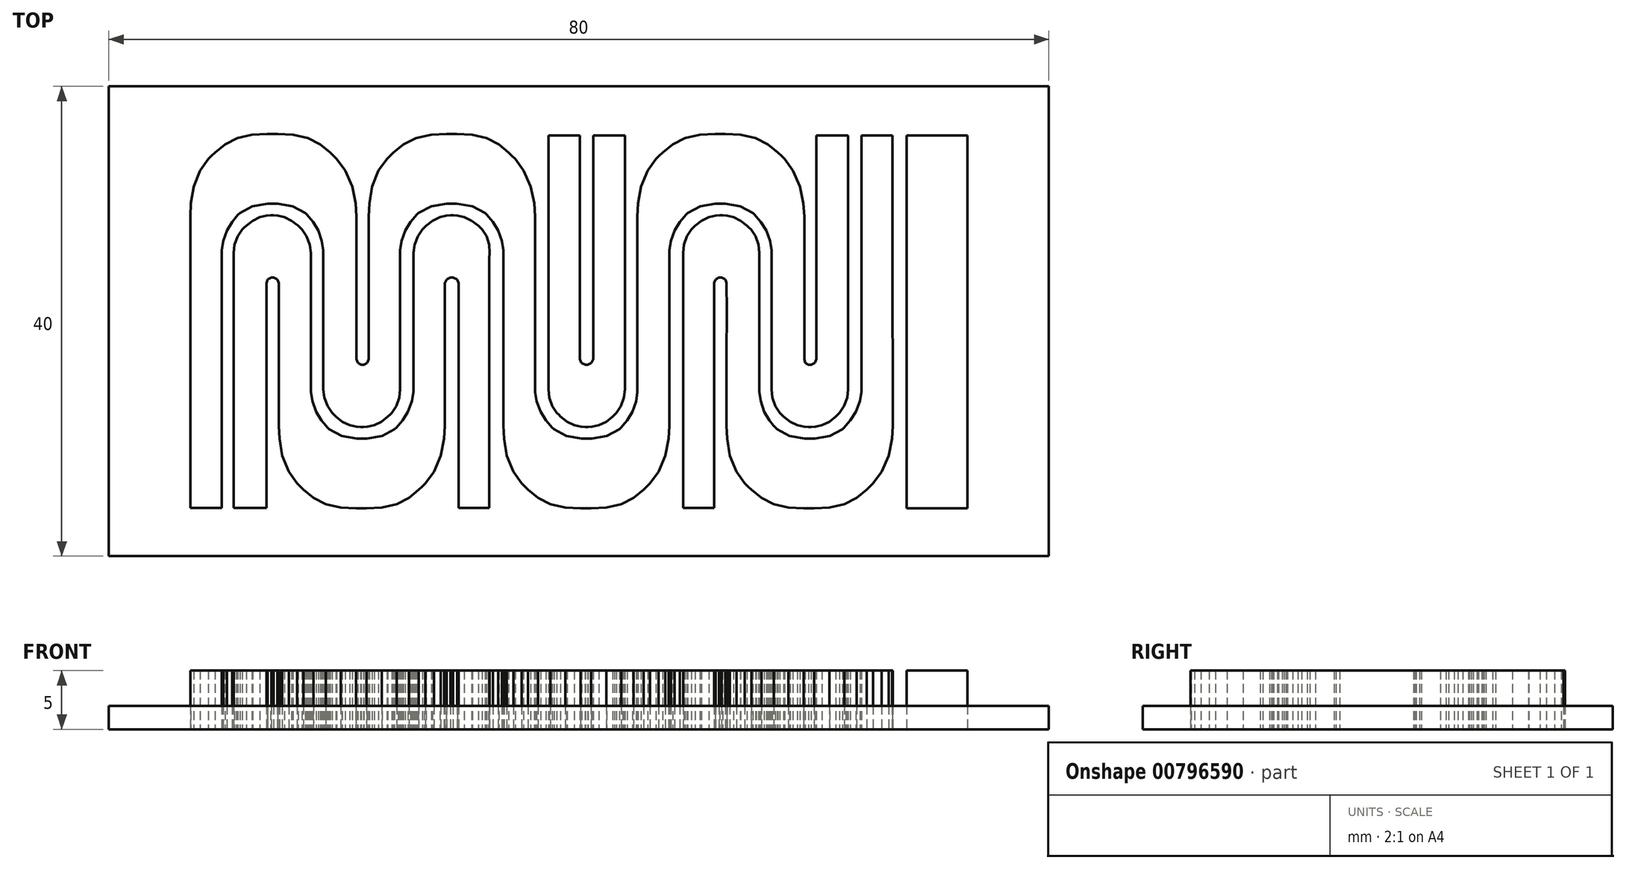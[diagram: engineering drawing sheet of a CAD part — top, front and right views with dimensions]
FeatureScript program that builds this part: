
annotation { "Feature Type Name" : "Feature", "Feature Type Description" : "" }
export const myFeature = defineFeature(function(context is Context, id is Id, definition is map)
    precondition{}
    {
        {
            var Q0;
            Q0=qCreatedBy(makeId("Top.planeOp"),FACE);
            var sketch = newSketch(context, id + "F0", { "sketchPlane" : qUnion([Q0])});
            skLineSegment(sketch, "E0.bottom", {"start": v(40, -20) * mm, "end": v(-40, -20) * mm});
            skLineSegment(sketch, "E0.top", {"start": v(40, 20) * mm, "end": v(-40, 20) * mm});
            skLineSegment(sketch, "E0.left", {"start": v(40, -20) * mm, "end": v(40, 20) * mm});
            skLineSegment(sketch, "E0.right", {"start": v(-40, -20) * mm, "end": v(-40, 20) * mm});
            skPoint(sketch, "E0.middle", {"position": v(0, 0) * mm});
            skSolve(sketch);
        }
        {
            var Q0;
            Q0 = qSketchRegion(id + "F0", true);
            extrude(context, id + "F1", {"entities" : qUnion([Q0]), "depth" : 2 * mm, "offsetDistance" : 25 * mm});
        }
        {
            var Q0;
            Q0=qCreatedBy(makeId("Top.planeOp"),FACE);
            var sketch = newSketch(context, id + "F2", { "sketchPlane" : qUnion([Q0])});
            skLineSegment(sketch, "E1", {"start": v(7.72, -8.54) * mm, "end": v(7.72, -4.96) * mm});
            skLineSegment(sketch, "E2", {"start": v(7.72, -4.96) * mm, "end": v(7.72, 3.1) * mm});
            skLineSegment(sketch, "E3", {"start": v(7.72, 3.1) * mm, "end": v(7.72, 5.78) * mm});
            skLineSegment(sketch, "E4", {"start": v(7.72, 5.78) * mm, "end": v(7.72, 6.04) * mm});
            skLineSegment(sketch, "E5", {"start": v(7.72, 6.04) * mm, "end": v(7.84, 6.84) * mm});
            skLineSegment(sketch, "E6", {"start": v(7.84, 6.84) * mm, "end": v(8.15, 7.73) * mm});
            skLineSegment(sketch, "E7", {"start": v(8.15, 7.73) * mm, "end": v(8.6, 8.46) * mm});
            skLineSegment(sketch, "E8", {"start": v(8.6, 8.46) * mm, "end": v(8.96, 8.9) * mm});
            skLineSegment(sketch, "E9", {"start": v(8.96, 8.9) * mm, "end": v(9.1, 9.04) * mm});
            skLineSegment(sketch, "E10", {"start": v(9.1, 9.04) * mm, "end": v(9.27, 9.21) * mm});
            skLineSegment(sketch, "E11", {"start": v(9.27, 9.21) * mm, "end": v(10.33, 9.79) * mm});
            skLineSegment(sketch, "E12", {"start": v(10.33, 9.79) * mm, "end": v(11.61, 10.02) * mm});
            skLineSegment(sketch, "E13", {"start": v(11.61, 10.02) * mm, "end": v(12.04, 10.02) * mm});
            skLineSegment(sketch, "E14", {"start": v(12.04, 10.02) * mm, "end": v(12.47, 10.02) * mm});
            skLineSegment(sketch, "E15", {"start": v(12.47, 10.02) * mm, "end": v(13.75, 9.79) * mm});
            skLineSegment(sketch, "E16", {"start": v(13.75, 9.79) * mm, "end": v(14.81, 9.21) * mm});
            skLineSegment(sketch, "E17", {"start": v(14.81, 9.21) * mm, "end": v(14.98, 9.04) * mm});
            skLineSegment(sketch, "E18", {"start": v(14.98, 9.04) * mm, "end": v(15.12, 8.9) * mm});
            skLineSegment(sketch, "E19", {"start": v(15.12, 8.9) * mm, "end": v(15.5, 8.46) * mm});
            skLineSegment(sketch, "E20", {"start": v(15.5, 8.46) * mm, "end": v(15.96, 7.73) * mm});
            skLineSegment(sketch, "E21", {"start": v(15.96, 7.73) * mm, "end": v(16.3, 6.84) * mm});
            skLineSegment(sketch, "E22", {"start": v(16.3, 6.84) * mm, "end": v(16.42, 6.04) * mm});
            skLineSegment(sketch, "E23", {"start": v(16.42, 6.04) * mm, "end": v(16.42, 5.78) * mm});
            skLineSegment(sketch, "E24", {"start": v(16.42, 5.78) * mm, "end": v(16.42, 3.05) * mm});
            skLineSegment(sketch, "E25", {"start": v(16.42, 3.05) * mm, "end": v(16.42, -3.1) * mm});
            skLineSegment(sketch, "E26", {"start": v(16.42, -3.1) * mm, "end": v(16.42, -5.15) * mm});
            skLineSegment(sketch, "E27", {"start": v(16.42, -5.15) * mm, "end": v(16.42, -5.3) * mm});
            skLineSegment(sketch, "E28", {"start": v(16.42, -5.3) * mm, "end": v(16.42, -5.79) * mm});
            skLineSegment(sketch, "E29", {"start": v(16.42, -5.79) * mm, "end": v(16.48, -6.49) * mm});
            skLineSegment(sketch, "E30", {"start": v(16.48, -6.49) * mm, "end": v(16.73, -7.22) * mm});
            skLineSegment(sketch, "E31", {"start": v(16.73, -7.22) * mm, "end": v(17.11, -7.81) * mm});
            skLineSegment(sketch, "E32", {"start": v(17.11, -7.81) * mm, "end": v(17.28, -7.97) * mm});
            skLineSegment(sketch, "E33", {"start": v(17.28, -7.97) * mm, "end": v(17.44, -8.13) * mm});
            skLineSegment(sketch, "E34", {"start": v(17.44, -8.13) * mm, "end": v(17.98, -8.55) * mm});
            skLineSegment(sketch, "E35", {"start": v(17.98, -8.55) * mm, "end": v(18.61, -8.86) * mm});
            skLineSegment(sketch, "E36", {"start": v(18.61, -8.86) * mm, "end": v(19.17, -8.98) * mm});
            skLineSegment(sketch, "E37", {"start": v(19.17, -8.98) * mm, "end": v(19.53, -9) * mm});
            skLineSegment(sketch, "E38", {"start": v(19.53, -9) * mm, "end": v(19.66, -9) * mm});
            skLineSegment(sketch, "E39", {"start": v(19.66, -9) * mm, "end": v(19.78, -9) * mm});
            skLineSegment(sketch, "E40", {"start": v(19.78, -9) * mm, "end": v(20.14, -8.98) * mm});
            skLineSegment(sketch, "E41", {"start": v(20.14, -8.98) * mm, "end": v(20.7, -8.86) * mm});
            skLineSegment(sketch, "E42", {"start": v(20.7, -8.86) * mm, "end": v(21.32, -8.55) * mm});
            skLineSegment(sketch, "E43", {"start": v(21.32, -8.55) * mm, "end": v(21.86, -8.13) * mm});
            skLineSegment(sketch, "E44", {"start": v(21.86, -8.13) * mm, "end": v(22.02, -7.97) * mm});
            skLineSegment(sketch, "E45", {"start": v(22.02, -7.97) * mm, "end": v(22.18, -7.81) * mm});
            skLineSegment(sketch, "E46", {"start": v(22.18, -7.81) * mm, "end": v(22.58, -7.22) * mm});
            skLineSegment(sketch, "E47", {"start": v(22.58, -7.22) * mm, "end": v(22.85, -6.49) * mm});
            skLineSegment(sketch, "E48", {"start": v(22.85, -6.49) * mm, "end": v(22.92, -5.79) * mm});
            skLineSegment(sketch, "E49", {"start": v(22.92, -5.79) * mm, "end": v(22.93, -5.3) * mm});
            skLineSegment(sketch, "E50", {"start": v(22.93, -5.3) * mm, "end": v(22.93, -5.15) * mm});
            skLineSegment(sketch, "E51", {"start": v(22.93, -5.15) * mm, "end": v(22.93, 0.1) * mm});
            skLineSegment(sketch, "E52", {"start": v(22.93, 0.1) * mm, "end": v(22.93, 11.89) * mm});
            skLineSegment(sketch, "E53", {"start": v(22.93, 11.89) * mm, "end": v(22.93, 15.82) * mm});
            skLineSegment(sketch, "E54", {"start": v(22.93, 15.82) * mm, "end": v(22.25, 15.82) * mm});
            skLineSegment(sketch, "E55", {"start": v(22.25, 15.82) * mm, "end": v(20.73, 15.82) * mm});
            skLineSegment(sketch, "E56", {"start": v(20.73, 15.82) * mm, "end": v(20.22, 15.82) * mm});
            skLineSegment(sketch, "E57", {"start": v(20.22, 15.82) * mm, "end": v(20.22, 13.45) * mm});
            skLineSegment(sketch, "E58", {"start": v(20.22, 13.45) * mm, "end": v(20.22, 6.35) * mm});
            skLineSegment(sketch, "E59", {"start": v(20.22, 6.35) * mm, "end": v(20.22, -0.75) * mm});
            skLineSegment(sketch, "E60", {"start": v(20.22, -0.75) * mm, "end": v(20.22, -3.12) * mm});
            skLineSegment(sketch, "E61", {"start": v(20.22, -3.12) * mm, "end": v(20.22, -3.22) * mm});
            skLineSegment(sketch, "E62", {"start": v(20.22, -3.22) * mm, "end": v(20.08, -3.54) * mm});
            skLineSegment(sketch, "E63", {"start": v(20.08, -3.54) * mm, "end": v(19.76, -3.71) * mm});
            skLineSegment(sketch, "E64", {"start": v(19.76, -3.71) * mm, "end": v(19.66, -3.71) * mm});
            skLineSegment(sketch, "E65", {"start": v(19.66, -3.71) * mm, "end": v(19.56, -3.71) * mm});
            skLineSegment(sketch, "E66", {"start": v(19.56, -3.71) * mm, "end": v(19.28, -3.54) * mm});
            skLineSegment(sketch, "E67", {"start": v(19.28, -3.54) * mm, "end": v(19.2, -3.22) * mm});
            skLineSegment(sketch, "E68", {"start": v(19.2, -3.22) * mm, "end": v(19.2, -3.12) * mm});
            skLineSegment(sketch, "E69", {"start": v(19.2, -3.12) * mm, "end": v(19.2, -2.43) * mm});
            skLineSegment(sketch, "E70", {"start": v(19.2, -2.43) * mm, "end": v(19.2, -0.37) * mm});
            skLineSegment(sketch, "E71", {"start": v(19.2, -0.37) * mm, "end": v(19.2, 2.78) * mm});
            skLineSegment(sketch, "E72", {"start": v(19.2, 2.78) * mm, "end": v(19.2, 5.9) * mm});
            skLineSegment(sketch, "E73", {"start": v(19.2, 5.9) * mm, "end": v(19.2, 7.9) * mm});
            skLineSegment(sketch, "E74", {"start": v(19.2, 7.9) * mm, "end": v(19.2, 8.57) * mm});
            skLineSegment(sketch, "E75", {"start": v(19.2, 8.57) * mm, "end": v(19.2, 8.93) * mm});
            skLineSegment(sketch, "E76", {"start": v(19.2, 8.93) * mm, "end": v(19.12, 10.03) * mm});
            skLineSegment(sketch, "E77", {"start": v(19.12, 10.03) * mm, "end": v(18.83, 11.47) * mm});
            skLineSegment(sketch, "E78", {"start": v(18.83, 11.47) * mm, "end": v(18.23, 12.84) * mm});
            skLineSegment(sketch, "E79", {"start": v(18.23, 12.84) * mm, "end": v(17.5, 13.82) * mm});
            skLineSegment(sketch, "E80", {"start": v(17.5, 13.82) * mm, "end": v(17.22, 14.1) * mm});
            skLineSegment(sketch, "E81", {"start": v(17.22, 14.1) * mm, "end": v(16.95, 14.35) * mm});
            skLineSegment(sketch, "E82", {"start": v(16.95, 14.35) * mm, "end": v(16.1, 15.05) * mm});
            skLineSegment(sketch, "E83", {"start": v(16.1, 15.05) * mm, "end": v(15.04, 15.6) * mm});
            skLineSegment(sketch, "E84", {"start": v(15.04, 15.6) * mm, "end": v(13.78, 15.87) * mm});
            skLineSegment(sketch, "E85", {"start": v(13.78, 15.87) * mm, "end": v(12.47, 15.94) * mm});
            skLineSegment(sketch, "E86", {"start": v(12.47, 15.94) * mm, "end": v(12.04, 15.94) * mm});
            skLineSegment(sketch, "E87", {"start": v(12.04, 15.94) * mm, "end": v(11.6, 15.94) * mm});
            skLineSegment(sketch, "E88", {"start": v(11.6, 15.94) * mm, "end": v(10.3, 15.87) * mm});
            skLineSegment(sketch, "E89", {"start": v(10.3, 15.87) * mm, "end": v(9.04, 15.6) * mm});
            skLineSegment(sketch, "E90", {"start": v(9.04, 15.6) * mm, "end": v(7.99, 15.05) * mm});
            skLineSegment(sketch, "E91", {"start": v(7.99, 15.05) * mm, "end": v(7.13, 14.35) * mm});
            skLineSegment(sketch, "E92", {"start": v(7.13, 14.35) * mm, "end": v(6.86, 14.1) * mm});
            skLineSegment(sketch, "E93", {"start": v(6.86, 14.1) * mm, "end": v(6.57, 13.82) * mm});
            skLineSegment(sketch, "E94", {"start": v(6.57, 13.82) * mm, "end": v(5.87, 12.84) * mm});
            skLineSegment(sketch, "E95", {"start": v(5.87, 12.84) * mm, "end": v(5.3, 11.47) * mm});
            skLineSegment(sketch, "E96", {"start": v(5.3, 11.47) * mm, "end": v(5.05, 10.03) * mm});
            skLineSegment(sketch, "E97", {"start": v(5.05, 10.03) * mm, "end": v(4.99, 8.93) * mm});
            skLineSegment(sketch, "E98", {"start": v(4.99, 8.93) * mm, "end": v(4.99, 8.57) * mm});
            skLineSegment(sketch, "E99", {"start": v(4.99, 8.57) * mm, "end": v(4.99, 8.14) * mm});
            skLineSegment(sketch, "E100", {"start": v(4.99, 8.14) * mm, "end": v(4.99, 6.85) * mm});
            skLineSegment(sketch, "E101", {"start": v(4.99, 6.85) * mm, "end": v(4.99, 4.77) * mm});
            skLineSegment(sketch, "E102", {"start": v(4.99, 4.77) * mm, "end": v(4.99, 2.5) * mm});
            skLineSegment(sketch, "E103", {"start": v(4.99, 2.5) * mm, "end": v(4.99, 0.23) * mm});
            skLineSegment(sketch, "E104", {"start": v(4.99, 0.23) * mm, "end": v(4.99, -1.9) * mm});
            skLineSegment(sketch, "E105", {"start": v(4.99, -1.9) * mm, "end": v(4.99, -3.73) * mm});
            skLineSegment(sketch, "E106", {"start": v(4.99, -3.73) * mm, "end": v(4.99, -5.07) * mm});
            skLineSegment(sketch, "E107", {"start": v(4.99, -5.07) * mm, "end": v(4.99, -5.58) * mm});
            skLineSegment(sketch, "E108", {"start": v(4.99, -5.58) * mm, "end": v(4.99, -5.75) * mm});
            skLineSegment(sketch, "E109", {"start": v(4.99, -5.75) * mm, "end": v(4.99, -6.01) * mm});
            skLineSegment(sketch, "E110", {"start": v(4.99, -6.01) * mm, "end": v(4.87, -6.8) * mm});
            skLineSegment(sketch, "E111", {"start": v(4.87, -6.8) * mm, "end": v(4.55, -7.7) * mm});
            skLineSegment(sketch, "E112", {"start": v(4.55, -7.7) * mm, "end": v(4.11, -8.44) * mm});
            skLineSegment(sketch, "E113", {"start": v(4.11, -8.44) * mm, "end": v(3.75, -8.9) * mm});
            skLineSegment(sketch, "E114", {"start": v(3.75, -8.9) * mm, "end": v(3.61, -9.03) * mm});
            skLineSegment(sketch, "E115", {"start": v(3.61, -9.03) * mm, "end": v(3.44, -9.2) * mm});
            skLineSegment(sketch, "E116", {"start": v(3.44, -9.2) * mm, "end": v(2.37, -9.77) * mm});
            skLineSegment(sketch, "E117", {"start": v(2.37, -9.77) * mm, "end": v(1.1, -10) * mm});
            skLineSegment(sketch, "E118", {"start": v(1.1, -10) * mm, "end": v(0.66, -10) * mm});
            skLineSegment(sketch, "E119", {"start": v(0.66, -10) * mm, "end": v(0.23, -10) * mm});
            skLineSegment(sketch, "E120", {"start": v(0.23, -10) * mm, "end": v(-1.06, -9.77) * mm});
            skLineSegment(sketch, "E121", {"start": v(-1.06, -9.77) * mm, "end": v(-2.11, -9.2) * mm});
            skLineSegment(sketch, "E122", {"start": v(-2.11, -9.2) * mm, "end": v(-2.28, -9.03) * mm});
            skLineSegment(sketch, "E123", {"start": v(-2.28, -9.03) * mm, "end": v(-2.42, -8.9) * mm});
            skLineSegment(sketch, "E124", {"start": v(-2.42, -8.9) * mm, "end": v(-2.8, -8.44) * mm});
            skLineSegment(sketch, "E125", {"start": v(-2.8, -8.44) * mm, "end": v(-3.26, -7.7) * mm});
            skLineSegment(sketch, "E126", {"start": v(-3.26, -7.7) * mm, "end": v(-3.6, -6.8) * mm});
            skLineSegment(sketch, "E127", {"start": v(-3.6, -6.8) * mm, "end": v(-3.72, -6.01) * mm});
            skLineSegment(sketch, "E128", {"start": v(-3.72, -6.01) * mm, "end": v(-3.72, -5.75) * mm});
            skLineSegment(sketch, "E129", {"start": v(-3.72, -5.75) * mm, "end": v(-3.72, -2.17) * mm});
            skLineSegment(sketch, "E130", {"start": v(-3.72, -2.17) * mm, "end": v(-3.72, 5.89) * mm});
            skLineSegment(sketch, "E131", {"start": v(-3.72, 5.89) * mm, "end": v(-3.72, 8.58) * mm});
            skLineSegment(sketch, "E132", {"start": v(-3.72, 8.58) * mm, "end": v(-3.72, 8.94) * mm});
            skLineSegment(sketch, "E133", {"start": v(-3.72, 8.94) * mm, "end": v(-3.8, 10.04) * mm});
            skLineSegment(sketch, "E134", {"start": v(-3.8, 10.04) * mm, "end": v(-4.1, 11.48) * mm});
            skLineSegment(sketch, "E135", {"start": v(-4.1, 11.48) * mm, "end": v(-4.7, 12.84) * mm});
            skLineSegment(sketch, "E136", {"start": v(-4.7, 12.84) * mm, "end": v(-5.42, 13.82) * mm});
            skLineSegment(sketch, "E137", {"start": v(-5.42, 13.82) * mm, "end": v(-5.71, 14.1) * mm});
            skLineSegment(sketch, "E138", {"start": v(-5.71, 14.1) * mm, "end": v(-5.98, 14.35) * mm});
            skLineSegment(sketch, "E139", {"start": v(-5.98, 14.35) * mm, "end": v(-6.82, 15.05) * mm});
            skLineSegment(sketch, "E140", {"start": v(-6.82, 15.05) * mm, "end": v(-7.84, 15.6) * mm});
            skLineSegment(sketch, "E141", {"start": v(-7.84, 15.6) * mm, "end": v(-9.07, 15.87) * mm});
            skLineSegment(sketch, "E142", {"start": v(-9.07, 15.87) * mm, "end": v(-10.38, 15.94) * mm});
            skLineSegment(sketch, "E143", {"start": v(-10.38, 15.94) * mm, "end": v(-10.8, 15.94) * mm});
            skLineSegment(sketch, "E144", {"start": v(-10.8, 15.94) * mm, "end": v(-11.25, 15.94) * mm});
            skLineSegment(sketch, "E145", {"start": v(-11.25, 15.94) * mm, "end": v(-12.56, 15.87) * mm});
            skLineSegment(sketch, "E146", {"start": v(-12.56, 15.87) * mm, "end": v(-13.85, 15.6) * mm});
            skLineSegment(sketch, "E147", {"start": v(-13.85, 15.6) * mm, "end": v(-14.92, 15.05) * mm});
            skLineSegment(sketch, "E148", {"start": v(-14.92, 15.05) * mm, "end": v(-15.79, 14.35) * mm});
            skLineSegment(sketch, "E149", {"start": v(-15.79, 14.35) * mm, "end": v(-16.05, 14.1) * mm});
            skLineSegment(sketch, "E150", {"start": v(-16.05, 14.1) * mm, "end": v(-16.34, 13.82) * mm});
            skLineSegment(sketch, "E151", {"start": v(-16.34, 13.82) * mm, "end": v(-17.04, 12.84) * mm});
            skLineSegment(sketch, "E152", {"start": v(-17.04, 12.84) * mm, "end": v(-17.6, 11.48) * mm});
            skLineSegment(sketch, "E153", {"start": v(-17.6, 11.48) * mm, "end": v(-17.83, 10.04) * mm});
            skLineSegment(sketch, "E154", {"start": v(-17.83, 10.04) * mm, "end": v(-17.88, 8.94) * mm});
            skLineSegment(sketch, "E155", {"start": v(-17.88, 8.94) * mm, "end": v(-17.88, 8.58) * mm});
            skLineSegment(sketch, "E156", {"start": v(-17.88, 8.58) * mm, "end": v(-17.88, 5.65) * mm});
            skLineSegment(sketch, "E157", {"start": v(-17.88, 5.65) * mm, "end": v(-17.88, -0.93) * mm});
            skLineSegment(sketch, "E158", {"start": v(-17.88, -0.93) * mm, "end": v(-17.88, -3.12) * mm});
            skLineSegment(sketch, "E159", {"start": v(-17.88, -3.12) * mm, "end": v(-17.88, -3.22) * mm});
            skLineSegment(sketch, "E160", {"start": v(-17.88, -3.22) * mm, "end": v(-18, -3.54) * mm});
            skLineSegment(sketch, "E161", {"start": v(-18, -3.54) * mm, "end": v(-18.3, -3.71) * mm});
            skLineSegment(sketch, "E162", {"start": v(-18.3, -3.71) * mm, "end": v(-18.4, -3.71) * mm});
            skLineSegment(sketch, "E163", {"start": v(-18.4, -3.71) * mm, "end": v(-18.5, -3.71) * mm});
            skLineSegment(sketch, "E164", {"start": v(-18.5, -3.71) * mm, "end": v(-18.82, -3.54) * mm});
            skLineSegment(sketch, "E165", {"start": v(-18.82, -3.54) * mm, "end": v(-18.94, -3.22) * mm});
            skLineSegment(sketch, "E166", {"start": v(-18.94, -3.22) * mm, "end": v(-18.94, -3.12) * mm});
            skLineSegment(sketch, "E167", {"start": v(-18.94, -3.12) * mm, "end": v(-18.94, -0.2) * mm});
            skLineSegment(sketch, "E168", {"start": v(-18.94, -0.2) * mm, "end": v(-18.94, 6.38) * mm});
            skLineSegment(sketch, "E169", {"start": v(-18.94, 6.38) * mm, "end": v(-18.94, 8.58) * mm});
            skLineSegment(sketch, "E170", {"start": v(-18.94, 8.58) * mm, "end": v(-18.94, 8.94) * mm});
            skLineSegment(sketch, "E171", {"start": v(-18.94, 8.94) * mm, "end": v(-19, 10.04) * mm});
            skLineSegment(sketch, "E172", {"start": v(-19, 10.04) * mm, "end": v(-19.3, 11.47) * mm});
            skLineSegment(sketch, "E173", {"start": v(-19.3, 11.47) * mm, "end": v(-19.89, 12.84) * mm});
            skLineSegment(sketch, "E174", {"start": v(-19.89, 12.84) * mm, "end": v(-20.6, 13.82) * mm});
            skLineSegment(sketch, "E175", {"start": v(-20.6, 13.82) * mm, "end": v(-20.9, 14.1) * mm});
            skLineSegment(sketch, "E176", {"start": v(-20.9, 14.1) * mm, "end": v(-21.17, 14.35) * mm});
            skLineSegment(sketch, "E177", {"start": v(-21.17, 14.35) * mm, "end": v(-22.02, 15.05) * mm});
            skLineSegment(sketch, "E178", {"start": v(-22.02, 15.05) * mm, "end": v(-23.07, 15.6) * mm});
            skLineSegment(sketch, "E179", {"start": v(-23.07, 15.6) * mm, "end": v(-24.33, 15.87) * mm});
            skLineSegment(sketch, "E180", {"start": v(-24.33, 15.87) * mm, "end": v(-25.64, 15.94) * mm});
            skLineSegment(sketch, "E181", {"start": v(-25.64, 15.94) * mm, "end": v(-26.08, 15.94) * mm});
            skLineSegment(sketch, "E182", {"start": v(-26.08, 15.94) * mm, "end": v(-26.51, 15.94) * mm});
            skLineSegment(sketch, "E183", {"start": v(-26.51, 15.94) * mm, "end": v(-27.82, 15.87) * mm});
            skLineSegment(sketch, "E184", {"start": v(-27.82, 15.87) * mm, "end": v(-29.07, 15.6) * mm});
            skLineSegment(sketch, "E185", {"start": v(-29.07, 15.6) * mm, "end": v(-30.12, 15.05) * mm});
            skLineSegment(sketch, "E186", {"start": v(-30.12, 15.05) * mm, "end": v(-30.98, 14.35) * mm});
            skLineSegment(sketch, "E187", {"start": v(-30.98, 14.35) * mm, "end": v(-31.24, 14.1) * mm});
            skLineSegment(sketch, "E188", {"start": v(-31.24, 14.1) * mm, "end": v(-31.53, 13.82) * mm});
            skLineSegment(sketch, "E189", {"start": v(-31.53, 13.82) * mm, "end": v(-32.24, 12.84) * mm});
            skLineSegment(sketch, "E190", {"start": v(-32.24, 12.84) * mm, "end": v(-32.79, 11.47) * mm});
            skLineSegment(sketch, "E191", {"start": v(-32.79, 11.47) * mm, "end": v(-33.02, 10.04) * mm});
            skLineSegment(sketch, "E192", {"start": v(-33.02, 10.04) * mm, "end": v(-33.07, 8.94) * mm});
            skLineSegment(sketch, "E193", {"start": v(-33.07, 8.94) * mm, "end": v(-33.07, 8.58) * mm});
            skLineSegment(sketch, "E194", {"start": v(-33.07, 8.58) * mm, "end": v(-33.07, -15.9) * mm});
            skLineSegment(sketch, "E195", {"start": v(-33.07, -15.9) * mm, "end": v(-32.4, -15.9) * mm});
            skLineSegment(sketch, "E196", {"start": v(-32.4, -15.9) * mm, "end": v(-30.9, -15.9) * mm});
            skLineSegment(sketch, "E197", {"start": v(-30.9, -15.9) * mm, "end": v(-30.4, -15.9) * mm});
            skLineSegment(sketch, "E198", {"start": v(-30.4, -15.9) * mm, "end": v(-30.4, -13.18) * mm});
            skLineSegment(sketch, "E199", {"start": v(-30.4, -13.18) * mm, "end": v(-30.4, -5.06) * mm});
            skLineSegment(sketch, "E200", {"start": v(-30.4, -5.06) * mm, "end": v(-30.4, 3.07) * mm});
            skLineSegment(sketch, "E201", {"start": v(-30.4, 3.07) * mm, "end": v(-30.4, 5.77) * mm});
            skLineSegment(sketch, "E202", {"start": v(-30.4, 5.77) * mm, "end": v(-30.4, 6.04) * mm});
            skLineSegment(sketch, "E203", {"start": v(-30.4, 6.04) * mm, "end": v(-30.27, 6.83) * mm});
            skLineSegment(sketch, "E204", {"start": v(-30.27, 6.83) * mm, "end": v(-29.96, 7.73) * mm});
            skLineSegment(sketch, "E205", {"start": v(-29.96, 7.73) * mm, "end": v(-29.52, 8.46) * mm});
            skLineSegment(sketch, "E206", {"start": v(-29.52, 8.46) * mm, "end": v(-29.15, 8.9) * mm});
            skLineSegment(sketch, "E207", {"start": v(-29.15, 8.9) * mm, "end": v(-29.01, 9.04) * mm});
            skLineSegment(sketch, "E208", {"start": v(-29.01, 9.04) * mm, "end": v(-28.85, 9.21) * mm});
            skLineSegment(sketch, "E209", {"start": v(-28.85, 9.21) * mm, "end": v(-27.78, 9.79) * mm});
            skLineSegment(sketch, "E210", {"start": v(-27.78, 9.79) * mm, "end": v(-26.5, 10.02) * mm});
            skLineSegment(sketch, "E211", {"start": v(-26.5, 10.02) * mm, "end": v(-26.07, 10.02) * mm});
            skLineSegment(sketch, "E212", {"start": v(-26.07, 10.02) * mm, "end": v(-25.64, 10.02) * mm});
            skLineSegment(sketch, "E213", {"start": v(-25.64, 10.02) * mm, "end": v(-24.35, 9.79) * mm});
            skLineSegment(sketch, "E214", {"start": v(-24.35, 9.79) * mm, "end": v(-23.29, 9.21) * mm});
            skLineSegment(sketch, "E215", {"start": v(-23.29, 9.21) * mm, "end": v(-23.12, 9.04) * mm});
            skLineSegment(sketch, "E216", {"start": v(-23.12, 9.04) * mm, "end": v(-22.98, 8.9) * mm});
            skLineSegment(sketch, "E217", {"start": v(-22.98, 8.9) * mm, "end": v(-22.62, 8.46) * mm});
            skLineSegment(sketch, "E218", {"start": v(-22.62, 8.46) * mm, "end": v(-22.18, 7.73) * mm});
            skLineSegment(sketch, "E219", {"start": v(-22.18, 7.73) * mm, "end": v(-21.87, 6.83) * mm});
            skLineSegment(sketch, "E220", {"start": v(-21.87, 6.83) * mm, "end": v(-21.75, 6.04) * mm});
            skLineSegment(sketch, "E221", {"start": v(-21.75, 6.04) * mm, "end": v(-21.75, 5.77) * mm});
            skLineSegment(sketch, "E222", {"start": v(-21.75, 5.77) * mm, "end": v(-21.75, 3.04) * mm});
            skLineSegment(sketch, "E223", {"start": v(-21.75, 3.04) * mm, "end": v(-21.75, -3.1) * mm});
            skLineSegment(sketch, "E224", {"start": v(-21.75, -3.1) * mm, "end": v(-21.75, -5.15) * mm});
            skLineSegment(sketch, "E225", {"start": v(-21.75, -5.15) * mm, "end": v(-21.75, -5.3) * mm});
            skLineSegment(sketch, "E226", {"start": v(-21.75, -5.3) * mm, "end": v(-21.75, -5.79) * mm});
            skLineSegment(sketch, "E227", {"start": v(-21.75, -5.79) * mm, "end": v(-21.66, -6.49) * mm});
            skLineSegment(sketch, "E228", {"start": v(-21.66, -6.49) * mm, "end": v(-21.39, -7.22) * mm});
            skLineSegment(sketch, "E229", {"start": v(-21.39, -7.22) * mm, "end": v(-21, -7.8) * mm});
            skLineSegment(sketch, "E230", {"start": v(-21, -7.8) * mm, "end": v(-20.83, -7.97) * mm});
            skLineSegment(sketch, "E231", {"start": v(-20.83, -7.97) * mm, "end": v(-20.67, -8.13) * mm});
            skLineSegment(sketch, "E232", {"start": v(-20.67, -8.13) * mm, "end": v(-20.12, -8.55) * mm});
            skLineSegment(sketch, "E233", {"start": v(-20.12, -8.55) * mm, "end": v(-19.5, -8.86) * mm});
            skLineSegment(sketch, "E234", {"start": v(-19.5, -8.86) * mm, "end": v(-18.94, -8.98) * mm});
            skLineSegment(sketch, "E235", {"start": v(-18.94, -8.98) * mm, "end": v(-18.58, -9) * mm});
            skLineSegment(sketch, "E236", {"start": v(-18.58, -9) * mm, "end": v(-18.46, -9) * mm});
            skLineSegment(sketch, "E237", {"start": v(-18.46, -9) * mm, "end": v(-18.34, -9) * mm});
            skLineSegment(sketch, "E238", {"start": v(-18.34, -9) * mm, "end": v(-17.98, -8.98) * mm});
            skLineSegment(sketch, "E239", {"start": v(-17.98, -8.98) * mm, "end": v(-17.42, -8.86) * mm});
            skLineSegment(sketch, "E240", {"start": v(-17.42, -8.86) * mm, "end": v(-16.8, -8.55) * mm});
            skLineSegment(sketch, "E241", {"start": v(-16.8, -8.55) * mm, "end": v(-16.25, -8.13) * mm});
            skLineSegment(sketch, "E242", {"start": v(-16.25, -8.13) * mm, "end": v(-16.09, -7.97) * mm});
            skLineSegment(sketch, "E243", {"start": v(-16.09, -7.97) * mm, "end": v(-15.93, -7.81) * mm});
            skLineSegment(sketch, "E244", {"start": v(-15.93, -7.81) * mm, "end": v(-15.53, -7.22) * mm});
            skLineSegment(sketch, "E245", {"start": v(-15.53, -7.22) * mm, "end": v(-15.28, -6.49) * mm});
            skLineSegment(sketch, "E246", {"start": v(-15.28, -6.49) * mm, "end": v(-15.2, -5.79) * mm});
            skLineSegment(sketch, "E247", {"start": v(-15.2, -5.79) * mm, "end": v(-15.2, -5.3) * mm});
            skLineSegment(sketch, "E248", {"start": v(-15.2, -5.3) * mm, "end": v(-15.2, -5.15) * mm});
            skLineSegment(sketch, "E249", {"start": v(-15.2, -5.15) * mm, "end": v(-15.2, -4.73) * mm});
            skLineSegment(sketch, "E250", {"start": v(-15.2, -4.73) * mm, "end": v(-15.2, -3.5) * mm});
            skLineSegment(sketch, "E251", {"start": v(-15.2, -3.5) * mm, "end": v(-15.2, -0.44) * mm});
            skLineSegment(sketch, "E252", {"start": v(-15.2, -0.44) * mm, "end": v(-15.2, 3) * mm});
            skLineSegment(sketch, "E253", {"start": v(-15.2, 3) * mm, "end": v(-15.2, 5.08) * mm});
            skLineSegment(sketch, "E254", {"start": v(-15.2, 5.08) * mm, "end": v(-15.2, 5.77) * mm});
            skLineSegment(sketch, "E255", {"start": v(-15.2, 5.77) * mm, "end": v(-15.2, 6.04) * mm});
            skLineSegment(sketch, "E256", {"start": v(-15.2, 6.04) * mm, "end": v(-15.08, 6.83) * mm});
            skLineSegment(sketch, "E257", {"start": v(-15.08, 6.83) * mm, "end": v(-14.77, 7.73) * mm});
            skLineSegment(sketch, "E258", {"start": v(-14.77, 7.73) * mm, "end": v(-14.32, 8.46) * mm});
            skLineSegment(sketch, "E259", {"start": v(-14.32, 8.46) * mm, "end": v(-13.96, 8.9) * mm});
            skLineSegment(sketch, "E260", {"start": v(-13.96, 8.9) * mm, "end": v(-13.82, 9.04) * mm});
            skLineSegment(sketch, "E261", {"start": v(-13.82, 9.04) * mm, "end": v(-13.65, 9.21) * mm});
            skLineSegment(sketch, "E262", {"start": v(-13.65, 9.21) * mm, "end": v(-12.56, 9.79) * mm});
            skLineSegment(sketch, "E263", {"start": v(-12.56, 9.79) * mm, "end": v(-11.25, 10.02) * mm});
            skLineSegment(sketch, "E264", {"start": v(-11.25, 10.02) * mm, "end": v(-10.8, 10.02) * mm});
            skLineSegment(sketch, "E265", {"start": v(-10.8, 10.02) * mm, "end": v(-10.38, 10.02) * mm});
            skLineSegment(sketch, "E266", {"start": v(-10.38, 10.02) * mm, "end": v(-9.07, 9.79) * mm});
            skLineSegment(sketch, "E267", {"start": v(-9.07, 9.79) * mm, "end": v(-7.98, 9.21) * mm});
            skLineSegment(sketch, "E268", {"start": v(-7.98, 9.21) * mm, "end": v(-7.81, 9.04) * mm});
            skLineSegment(sketch, "E269", {"start": v(-7.81, 9.04) * mm, "end": v(-7.68, 8.9) * mm});
            skLineSegment(sketch, "E270", {"start": v(-7.68, 8.9) * mm, "end": v(-7.3, 8.46) * mm});
            skLineSegment(sketch, "E271", {"start": v(-7.3, 8.46) * mm, "end": v(-6.86, 7.73) * mm});
            skLineSegment(sketch, "E272", {"start": v(-6.86, 7.73) * mm, "end": v(-6.54, 6.83) * mm});
            skLineSegment(sketch, "E273", {"start": v(-6.54, 6.83) * mm, "end": v(-6.42, 6.04) * mm});
            skLineSegment(sketch, "E274", {"start": v(-6.42, 6.04) * mm, "end": v(-6.42, 5.77) * mm});
            skLineSegment(sketch, "E275", {"start": v(-6.42, 5.77) * mm, "end": v(-6.42, 2.2) * mm});
            skLineSegment(sketch, "E276", {"start": v(-6.42, 2.2) * mm, "end": v(-6.42, -5.84) * mm});
            skLineSegment(sketch, "E277", {"start": v(-6.42, -5.84) * mm, "end": v(-6.42, -8.53) * mm});
            skLineSegment(sketch, "E278", {"start": v(-6.42, -8.53) * mm, "end": v(-6.42, -8.9) * mm});
            skLineSegment(sketch, "E279", {"start": v(-6.42, -8.9) * mm, "end": v(-6.37, -10) * mm});
            skLineSegment(sketch, "E280", {"start": v(-6.37, -10) * mm, "end": v(-6.12, -11.46) * mm});
            skLineSegment(sketch, "E281", {"start": v(-6.12, -11.46) * mm, "end": v(-5.57, -12.83) * mm});
            skLineSegment(sketch, "E282", {"start": v(-5.57, -12.83) * mm, "end": v(-4.87, -13.81) * mm});
            skLineSegment(sketch, "E283", {"start": v(-4.87, -13.81) * mm, "end": v(-4.58, -14.08) * mm});
            skLineSegment(sketch, "E284", {"start": v(-4.58, -14.08) * mm, "end": v(-4.32, -14.34) * mm});
            skLineSegment(sketch, "E285", {"start": v(-4.32, -14.34) * mm, "end": v(-3.46, -15.04) * mm});
            skLineSegment(sketch, "E286", {"start": v(-3.46, -15.04) * mm, "end": v(-2.4, -15.6) * mm});
            skLineSegment(sketch, "E287", {"start": v(-2.4, -15.6) * mm, "end": v(-1.15, -15.86) * mm});
            skLineSegment(sketch, "E288", {"start": v(-1.15, -15.86) * mm, "end": v(0.16, -15.93) * mm});
            skLineSegment(sketch, "E289", {"start": v(0.16, -15.93) * mm, "end": v(0.6, -15.93) * mm});
            skLineSegment(sketch, "E290", {"start": v(0.6, -15.93) * mm, "end": v(1.03, -15.93) * mm});
            skLineSegment(sketch, "E291", {"start": v(1.03, -15.93) * mm, "end": v(2.34, -15.86) * mm});
            skLineSegment(sketch, "E292", {"start": v(2.34, -15.86) * mm, "end": v(3.6, -15.6) * mm});
            skLineSegment(sketch, "E293", {"start": v(3.6, -15.6) * mm, "end": v(4.65, -15.04) * mm});
            skLineSegment(sketch, "E294", {"start": v(4.65, -15.04) * mm, "end": v(5.5, -14.34) * mm});
            skLineSegment(sketch, "E295", {"start": v(5.5, -14.34) * mm, "end": v(5.77, -14.08) * mm});
            skLineSegment(sketch, "E296", {"start": v(5.77, -14.08) * mm, "end": v(6.06, -13.81) * mm});
            skLineSegment(sketch, "E297", {"start": v(6.06, -13.81) * mm, "end": v(6.78, -12.83) * mm});
            skLineSegment(sketch, "E298", {"start": v(6.78, -12.83) * mm, "end": v(7.37, -11.46) * mm});
            skLineSegment(sketch, "E299", {"start": v(7.37, -11.46) * mm, "end": v(7.65, -10) * mm});
            skLineSegment(sketch, "E300", {"start": v(7.65, -10) * mm, "end": v(7.72, -8.9) * mm});
            skLineSegment(sketch, "E301", {"start": v(7.72, -8.9) * mm, "end": v(7.72, -8.54) * mm});
            skLineSegment(sketch, "E302", {"start": v(24.76, -14.08) * mm, "end": v(25.05, -13.81) * mm});
            skLineSegment(sketch, "E303", {"start": v(25.05, -13.81) * mm, "end": v(25.77, -12.83) * mm});
            skLineSegment(sketch, "E304", {"start": v(25.77, -12.83) * mm, "end": v(26.37, -11.46) * mm});
            skLineSegment(sketch, "E305", {"start": v(26.37, -11.46) * mm, "end": v(26.65, -10) * mm});
            skLineSegment(sketch, "E306", {"start": v(26.65, -10) * mm, "end": v(26.73, -8.9) * mm});
            skLineSegment(sketch, "E307", {"start": v(26.73, -8.9) * mm, "end": v(26.73, -8.54) * mm});
            skLineSegment(sketch, "E308", {"start": v(26.73, -8.54) * mm, "end": v(26.72, -6.55) * mm});
            skLineSegment(sketch, "E309", {"start": v(26.72, -6.55) * mm, "end": v(26.7, 3.64) * mm});
            skLineSegment(sketch, "E310", {"start": v(26.7, 3.64) * mm, "end": v(26.7, 12.77) * mm});
            skLineSegment(sketch, "E311", {"start": v(26.7, 12.77) * mm, "end": v(26.7, 15.82) * mm});
            skLineSegment(sketch, "E312", {"start": v(26.7, 15.82) * mm, "end": v(26.04, 15.82) * mm});
            skLineSegment(sketch, "E313", {"start": v(26.04, 15.82) * mm, "end": v(24.56, 15.82) * mm});
            skLineSegment(sketch, "E314", {"start": v(24.56, 15.82) * mm, "end": v(24.06, 15.82) * mm});
            skLineSegment(sketch, "E315", {"start": v(24.06, 15.82) * mm, "end": v(24.06, 13.12) * mm});
            skLineSegment(sketch, "E316", {"start": v(24.06, 13.12) * mm, "end": v(24.06, 5.04) * mm});
            skLineSegment(sketch, "E317", {"start": v(24.06, 5.04) * mm, "end": v(24.06, -3.04) * mm});
            skLineSegment(sketch, "E318", {"start": v(24.06, -3.04) * mm, "end": v(24.06, -5.74) * mm});
            skLineSegment(sketch, "E319", {"start": v(24.06, -5.74) * mm, "end": v(24.06, -6) * mm});
            skLineSegment(sketch, "E320", {"start": v(24.06, -6) * mm, "end": v(23.93, -6.8) * mm});
            skLineSegment(sketch, "E321", {"start": v(23.93, -6.8) * mm, "end": v(23.58, -7.7) * mm});
            skLineSegment(sketch, "E322", {"start": v(23.58, -7.7) * mm, "end": v(23.12, -8.44) * mm});
            skLineSegment(sketch, "E323", {"start": v(23.12, -8.44) * mm, "end": v(22.74, -8.9) * mm});
            skLineSegment(sketch, "E324", {"start": v(22.74, -8.9) * mm, "end": v(22.6, -9.03) * mm});
            skLineSegment(sketch, "E325", {"start": v(22.6, -9.03) * mm, "end": v(22.43, -9.2) * mm});
            skLineSegment(sketch, "E326", {"start": v(22.43, -9.2) * mm, "end": v(21.37, -9.77) * mm});
            skLineSegment(sketch, "E327", {"start": v(21.37, -9.77) * mm, "end": v(20.08, -10) * mm});
            skLineSegment(sketch, "E328", {"start": v(20.08, -10) * mm, "end": v(19.66, -10) * mm});
            skLineSegment(sketch, "E329", {"start": v(19.66, -10) * mm, "end": v(19.23, -10) * mm});
            skLineSegment(sketch, "E330", {"start": v(19.23, -10) * mm, "end": v(17.94, -9.77) * mm});
            skLineSegment(sketch, "E331", {"start": v(17.94, -9.77) * mm, "end": v(16.88, -9.2) * mm});
            skLineSegment(sketch, "E332", {"start": v(16.88, -9.2) * mm, "end": v(16.7, -9.03) * mm});
            skLineSegment(sketch, "E333", {"start": v(16.7, -9.03) * mm, "end": v(16.57, -8.9) * mm});
            skLineSegment(sketch, "E334", {"start": v(16.57, -8.9) * mm, "end": v(16.2, -8.44) * mm});
            skLineSegment(sketch, "E335", {"start": v(16.2, -8.44) * mm, "end": v(15.78, -7.7) * mm});
            skLineSegment(sketch, "E336", {"start": v(15.78, -7.7) * mm, "end": v(15.48, -6.8) * mm});
            skLineSegment(sketch, "E337", {"start": v(15.48, -6.8) * mm, "end": v(15.36, -6) * mm});
            skLineSegment(sketch, "E338", {"start": v(15.36, -6) * mm, "end": v(15.36, -5.74) * mm});
            skLineSegment(sketch, "E339", {"start": v(15.36, -5.74) * mm, "end": v(15.36, -4.37) * mm});
            skLineSegment(sketch, "E340", {"start": v(15.36, -4.37) * mm, "end": v(15.36, -0.27) * mm});
            skLineSegment(sketch, "E341", {"start": v(15.36, -0.27) * mm, "end": v(15.36, 3.82) * mm});
            skLineSegment(sketch, "E342", {"start": v(15.36, 3.82) * mm, "end": v(15.36, 5.18) * mm});
            skLineSegment(sketch, "E343", {"start": v(15.36, 5.18) * mm, "end": v(15.36, 5.34) * mm});
            skLineSegment(sketch, "E344", {"start": v(15.36, 5.34) * mm, "end": v(15.37, 5.82) * mm});
            skLineSegment(sketch, "E345", {"start": v(15.37, 5.82) * mm, "end": v(15.3, 6.51) * mm});
            skLineSegment(sketch, "E346", {"start": v(15.3, 6.51) * mm, "end": v(15.04, 7.24) * mm});
            skLineSegment(sketch, "E347", {"start": v(15.04, 7.24) * mm, "end": v(14.65, 7.82) * mm});
            skLineSegment(sketch, "E348", {"start": v(14.65, 7.82) * mm, "end": v(14.48, 7.98) * mm});
            skLineSegment(sketch, "E349", {"start": v(14.48, 7.98) * mm, "end": v(14.32, 8.14) * mm});
            skLineSegment(sketch, "E350", {"start": v(14.32, 8.14) * mm, "end": v(13.78, 8.56) * mm});
            skLineSegment(sketch, "E351", {"start": v(13.78, 8.56) * mm, "end": v(13.16, 8.87) * mm});
            skLineSegment(sketch, "E352", {"start": v(13.16, 8.87) * mm, "end": v(12.6, 9) * mm});
            skLineSegment(sketch, "E353", {"start": v(12.6, 9) * mm, "end": v(12.24, 9.02) * mm});
            skLineSegment(sketch, "E354", {"start": v(12.24, 9.02) * mm, "end": v(12.12, 9.02) * mm});
            skLineSegment(sketch, "E355", {"start": v(12.12, 9.02) * mm, "end": v(12, 9.02) * mm});
            skLineSegment(sketch, "E356", {"start": v(12, 9.02) * mm, "end": v(11.64, 9) * mm});
            skLineSegment(sketch, "E357", {"start": v(11.64, 9) * mm, "end": v(11.08, 8.87) * mm});
            skLineSegment(sketch, "E358", {"start": v(11.08, 8.87) * mm, "end": v(10.45, 8.56) * mm});
            skLineSegment(sketch, "E359", {"start": v(10.45, 8.56) * mm, "end": v(9.9, 8.14) * mm});
            skLineSegment(sketch, "E360", {"start": v(9.9, 8.14) * mm, "end": v(9.75, 7.98) * mm});
            skLineSegment(sketch, "E361", {"start": v(9.75, 7.98) * mm, "end": v(9.59, 7.82) * mm});
            skLineSegment(sketch, "E362", {"start": v(9.59, 7.82) * mm, "end": v(9.2, 7.24) * mm});
            skLineSegment(sketch, "E363", {"start": v(9.2, 7.24) * mm, "end": v(8.95, 6.51) * mm});
            skLineSegment(sketch, "E364", {"start": v(8.95, 6.51) * mm, "end": v(8.89, 5.82) * mm});
            skLineSegment(sketch, "E365", {"start": v(8.89, 5.82) * mm, "end": v(8.9, 5.34) * mm});
            skLineSegment(sketch, "E366", {"start": v(8.9, 5.34) * mm, "end": v(8.9, 5.18) * mm});
            skLineSegment(sketch, "E367", {"start": v(8.9, 5.18) * mm, "end": v(8.9, -0.09) * mm});
            skLineSegment(sketch, "E368", {"start": v(8.9, -0.09) * mm, "end": v(8.9, -11.94) * mm});
            skLineSegment(sketch, "E369", {"start": v(8.9, -11.94) * mm, "end": v(8.9, -15.9) * mm});
            skLineSegment(sketch, "E370", {"start": v(8.9, -15.9) * mm, "end": v(9.22, -15.9) * mm});
            skLineSegment(sketch, "E371", {"start": v(9.22, -15.9) * mm, "end": v(10.2, -15.9) * mm});
            skLineSegment(sketch, "E372", {"start": v(10.2, -15.9) * mm, "end": v(11.18, -15.9) * mm});
            skLineSegment(sketch, "E373", {"start": v(11.18, -15.9) * mm, "end": v(11.5, -15.9) * mm});
            skLineSegment(sketch, "E374", {"start": v(11.5, -15.9) * mm, "end": v(11.5, -13.5) * mm});
            skLineSegment(sketch, "E375", {"start": v(11.5, -13.5) * mm, "end": v(11.5, -6.36) * mm});
            skLineSegment(sketch, "E376", {"start": v(11.5, -6.36) * mm, "end": v(11.5, 0.79) * mm});
            skLineSegment(sketch, "E377", {"start": v(11.5, 0.79) * mm, "end": v(11.5, 3.17) * mm});
            skLineSegment(sketch, "E378", {"start": v(11.5, 3.17) * mm, "end": v(11.5, 3.27) * mm});
            skLineSegment(sketch, "E379", {"start": v(11.5, 3.27) * mm, "end": v(11.63, 3.57) * mm});
            skLineSegment(sketch, "E380", {"start": v(11.63, 3.57) * mm, "end": v(11.94, 3.72) * mm});
            skLineSegment(sketch, "E381", {"start": v(11.94, 3.72) * mm, "end": v(12.04, 3.72) * mm});
            skLineSegment(sketch, "E382", {"start": v(12.04, 3.72) * mm, "end": v(12.15, 3.72) * mm});
            skLineSegment(sketch, "E383", {"start": v(12.15, 3.72) * mm, "end": v(12.45, 3.57) * mm});
            skLineSegment(sketch, "E384", {"start": v(12.45, 3.57) * mm, "end": v(12.57, 3.27) * mm});
            skLineSegment(sketch, "E385", {"start": v(12.57, 3.27) * mm, "end": v(12.57, 3.17) * mm});
            skLineSegment(sketch, "E386", {"start": v(12.57, 3.17) * mm, "end": v(12.58, 3.06) * mm});
            skLineSegment(sketch, "E387", {"start": v(12.58, 3.06) * mm, "end": v(12.58, 2.64) * mm});
            skLineSegment(sketch, "E388", {"start": v(12.58, 2.64) * mm, "end": v(12.58, 1.5) * mm});
            skLineSegment(sketch, "E389", {"start": v(12.58, 1.5) * mm, "end": v(12.58, -0.08) * mm});
            skLineSegment(sketch, "E390", {"start": v(12.58, -0.08) * mm, "end": v(12.58, -1.92) * mm});
            skLineSegment(sketch, "E391", {"start": v(12.58, -1.92) * mm, "end": v(12.58, -3.87) * mm});
            skLineSegment(sketch, "E392", {"start": v(12.58, -3.87) * mm, "end": v(12.57, -5.73) * mm});
            skLineSegment(sketch, "E393", {"start": v(12.57, -5.73) * mm, "end": v(12.57, -7.34) * mm});
            skLineSegment(sketch, "E394", {"start": v(12.57, -7.34) * mm, "end": v(12.57, -8.24) * mm});
            skLineSegment(sketch, "E395", {"start": v(12.57, -8.24) * mm, "end": v(12.57, -8.54) * mm});
            skLineSegment(sketch, "E396", {"start": v(12.57, -8.54) * mm, "end": v(12.57, -8.9) * mm});
            skLineSegment(sketch, "E397", {"start": v(12.57, -8.9) * mm, "end": v(12.62, -10) * mm});
            skLineSegment(sketch, "E398", {"start": v(12.62, -10) * mm, "end": v(12.87, -11.46) * mm});
            skLineSegment(sketch, "E399", {"start": v(12.87, -11.46) * mm, "end": v(13.42, -12.83) * mm});
            skLineSegment(sketch, "E400", {"start": v(13.42, -12.83) * mm, "end": v(14.12, -13.81) * mm});
            skLineSegment(sketch, "E401", {"start": v(14.12, -13.81) * mm, "end": v(14.4, -14.08) * mm});
            skLineSegment(sketch, "E402", {"start": v(14.4, -14.08) * mm, "end": v(14.68, -14.34) * mm});
            skLineSegment(sketch, "E403", {"start": v(14.68, -14.34) * mm, "end": v(15.54, -15.04) * mm});
            skLineSegment(sketch, "E404", {"start": v(15.54, -15.04) * mm, "end": v(16.59, -15.6) * mm});
            skLineSegment(sketch, "E405", {"start": v(16.59, -15.6) * mm, "end": v(17.85, -15.86) * mm});
            skLineSegment(sketch, "E406", {"start": v(17.85, -15.86) * mm, "end": v(19.15, -15.93) * mm});
            skLineSegment(sketch, "E407", {"start": v(19.15, -15.93) * mm, "end": v(19.59, -15.93) * mm});
            skLineSegment(sketch, "E408", {"start": v(19.59, -15.93) * mm, "end": v(20.02, -15.93) * mm});
            skLineSegment(sketch, "E409", {"start": v(20.02, -15.93) * mm, "end": v(21.33, -15.86) * mm});
            skLineSegment(sketch, "E410", {"start": v(21.33, -15.86) * mm, "end": v(22.59, -15.6) * mm});
            skLineSegment(sketch, "E411", {"start": v(22.59, -15.6) * mm, "end": v(23.64, -15.04) * mm});
            skLineSegment(sketch, "E412", {"start": v(23.64, -15.04) * mm, "end": v(24.5, -14.34) * mm});
            skLineSegment(sketch, "E413", {"start": v(24.5, -14.34) * mm, "end": v(24.76, -14.08) * mm});
            skLineSegment(sketch, "E414", {"start": v(-7.61, 5.18) * mm, "end": v(-7.61, 5.34) * mm});
            skLineSegment(sketch, "E415", {"start": v(-7.61, 5.34) * mm, "end": v(-7.6, 5.82) * mm});
            skLineSegment(sketch, "E416", {"start": v(-7.6, 5.82) * mm, "end": v(-7.64, 6.52) * mm});
            skLineSegment(sketch, "E417", {"start": v(-7.64, 6.52) * mm, "end": v(-7.86, 7.24) * mm});
            skLineSegment(sketch, "E418", {"start": v(-7.86, 7.24) * mm, "end": v(-8.24, 7.82) * mm});
            skLineSegment(sketch, "E419", {"start": v(-8.24, 7.82) * mm, "end": v(-8.4, 7.98) * mm});
            skLineSegment(sketch, "E420", {"start": v(-8.4, 7.98) * mm, "end": v(-8.56, 8.14) * mm});
            skLineSegment(sketch, "E421", {"start": v(-8.56, 8.14) * mm, "end": v(-9.11, 8.56) * mm});
            skLineSegment(sketch, "E422", {"start": v(-9.11, 8.56) * mm, "end": v(-9.75, 8.87) * mm});
            skLineSegment(sketch, "E423", {"start": v(-9.75, 8.87) * mm, "end": v(-10.32, 9) * mm});
            skLineSegment(sketch, "E424", {"start": v(-10.32, 9) * mm, "end": v(-10.69, 9.02) * mm});
            skLineSegment(sketch, "E425", {"start": v(-10.69, 9.02) * mm, "end": v(-10.8, 9.02) * mm});
            skLineSegment(sketch, "E426", {"start": v(-10.8, 9.02) * mm, "end": v(-10.93, 9.02) * mm});
            skLineSegment(sketch, "E427", {"start": v(-10.93, 9.02) * mm, "end": v(-11.29, 9) * mm});
            skLineSegment(sketch, "E428", {"start": v(-11.29, 9) * mm, "end": v(-11.83, 8.87) * mm});
            skLineSegment(sketch, "E429", {"start": v(-11.83, 8.87) * mm, "end": v(-12.44, 8.56) * mm});
            skLineSegment(sketch, "E430", {"start": v(-12.44, 8.56) * mm, "end": v(-12.98, 8.14) * mm});
            skLineSegment(sketch, "E431", {"start": v(-12.98, 8.14) * mm, "end": v(-13.14, 7.98) * mm});
            skLineSegment(sketch, "E432", {"start": v(-13.14, 7.98) * mm, "end": v(-13.3, 7.82) * mm});
            skLineSegment(sketch, "E433", {"start": v(-13.3, 7.82) * mm, "end": v(-13.7, 7.24) * mm});
            skLineSegment(sketch, "E434", {"start": v(-13.7, 7.24) * mm, "end": v(-13.98, 6.52) * mm});
            skLineSegment(sketch, "E435", {"start": v(-13.98, 6.52) * mm, "end": v(-14.07, 5.82) * mm});
            skLineSegment(sketch, "E436", {"start": v(-14.07, 5.82) * mm, "end": v(-14.08, 5.34) * mm});
            skLineSegment(sketch, "E437", {"start": v(-14.08, 5.34) * mm, "end": v(-14.08, 5.18) * mm});
            skLineSegment(sketch, "E438", {"start": v(-14.08, 5.18) * mm, "end": v(-14.08, 2.45) * mm});
            skLineSegment(sketch, "E439", {"start": v(-14.08, 2.45) * mm, "end": v(-14.08, -3.7) * mm});
            skLineSegment(sketch, "E440", {"start": v(-14.08, -3.7) * mm, "end": v(-14.08, -5.74) * mm});
            skLineSegment(sketch, "E441", {"start": v(-14.08, -5.74) * mm, "end": v(-14.08, -6) * mm});
            skLineSegment(sketch, "E442", {"start": v(-14.08, -6) * mm, "end": v(-14.2, -6.8) * mm});
            skLineSegment(sketch, "E443", {"start": v(-14.2, -6.8) * mm, "end": v(-14.54, -7.7) * mm});
            skLineSegment(sketch, "E444", {"start": v(-14.54, -7.7) * mm, "end": v(-15, -8.44) * mm});
            skLineSegment(sketch, "E445", {"start": v(-15, -8.44) * mm, "end": v(-15.38, -8.9) * mm});
            skLineSegment(sketch, "E446", {"start": v(-15.38, -8.9) * mm, "end": v(-15.51, -9.03) * mm});
            skLineSegment(sketch, "E447", {"start": v(-15.51, -9.03) * mm, "end": v(-15.68, -9.2) * mm});
            skLineSegment(sketch, "E448", {"start": v(-15.68, -9.2) * mm, "end": v(-16.74, -9.77) * mm});
            skLineSegment(sketch, "E449", {"start": v(-16.74, -9.77) * mm, "end": v(-18.03, -10) * mm});
            skLineSegment(sketch, "E450", {"start": v(-18.03, -10) * mm, "end": v(-18.46, -10) * mm});
            skLineSegment(sketch, "E451", {"start": v(-18.46, -10) * mm, "end": v(-18.9, -10) * mm});
            skLineSegment(sketch, "E452", {"start": v(-18.9, -10) * mm, "end": v(-20.17, -9.77) * mm});
            skLineSegment(sketch, "E453", {"start": v(-20.17, -9.77) * mm, "end": v(-21.24, -9.2) * mm});
            skLineSegment(sketch, "E454", {"start": v(-21.24, -9.2) * mm, "end": v(-21.4, -9.03) * mm});
            skLineSegment(sketch, "E455", {"start": v(-21.4, -9.03) * mm, "end": v(-21.54, -8.9) * mm});
            skLineSegment(sketch, "E456", {"start": v(-21.54, -8.9) * mm, "end": v(-21.9, -8.44) * mm});
            skLineSegment(sketch, "E457", {"start": v(-21.9, -8.44) * mm, "end": v(-22.36, -7.7) * mm});
            skLineSegment(sketch, "E458", {"start": v(-22.36, -7.7) * mm, "end": v(-22.68, -6.8) * mm});
            skLineSegment(sketch, "E459", {"start": v(-22.68, -6.8) * mm, "end": v(-22.8, -6) * mm});
            skLineSegment(sketch, "E460", {"start": v(-22.8, -6) * mm, "end": v(-22.8, -5.74) * mm});
            skLineSegment(sketch, "E461", {"start": v(-22.8, -5.74) * mm, "end": v(-22.8, -4.38) * mm});
            skLineSegment(sketch, "E462", {"start": v(-22.8, -4.38) * mm, "end": v(-22.8, -0.28) * mm});
            skLineSegment(sketch, "E463", {"start": v(-22.8, -0.28) * mm, "end": v(-22.8, 3.82) * mm});
            skLineSegment(sketch, "E464", {"start": v(-22.8, 3.82) * mm, "end": v(-22.8, 5.18) * mm});
            skLineSegment(sketch, "E465", {"start": v(-22.8, 5.18) * mm, "end": v(-22.8, 5.34) * mm});
            skLineSegment(sketch, "E466", {"start": v(-22.8, 5.34) * mm, "end": v(-22.8, 5.82) * mm});
            skLineSegment(sketch, "E467", {"start": v(-22.8, 5.82) * mm, "end": v(-22.9, 6.51) * mm});
            skLineSegment(sketch, "E468", {"start": v(-22.9, 6.51) * mm, "end": v(-23.18, 7.24) * mm});
            skLineSegment(sketch, "E469", {"start": v(-23.18, 7.24) * mm, "end": v(-23.57, 7.82) * mm});
            skLineSegment(sketch, "E470", {"start": v(-23.57, 7.82) * mm, "end": v(-23.74, 7.98) * mm});
            skLineSegment(sketch, "E471", {"start": v(-23.74, 7.98) * mm, "end": v(-23.9, 8.14) * mm});
            skLineSegment(sketch, "E472", {"start": v(-23.9, 8.14) * mm, "end": v(-24.44, 8.56) * mm});
            skLineSegment(sketch, "E473", {"start": v(-24.44, 8.56) * mm, "end": v(-25.07, 8.87) * mm});
            skLineSegment(sketch, "E474", {"start": v(-25.07, 8.87) * mm, "end": v(-25.62, 9) * mm});
            skLineSegment(sketch, "E475", {"start": v(-25.62, 9) * mm, "end": v(-25.98, 9.02) * mm});
            skLineSegment(sketch, "E476", {"start": v(-25.98, 9.02) * mm, "end": v(-26.1, 9.02) * mm});
            skLineSegment(sketch, "E477", {"start": v(-26.1, 9.02) * mm, "end": v(-26.22, 9.02) * mm});
            skLineSegment(sketch, "E478", {"start": v(-26.22, 9.02) * mm, "end": v(-26.59, 9) * mm});
            skLineSegment(sketch, "E479", {"start": v(-26.59, 9) * mm, "end": v(-27.14, 8.87) * mm});
            skLineSegment(sketch, "E480", {"start": v(-27.14, 8.87) * mm, "end": v(-27.77, 8.56) * mm});
            skLineSegment(sketch, "E481", {"start": v(-27.77, 8.56) * mm, "end": v(-28.31, 8.14) * mm});
            skLineSegment(sketch, "E482", {"start": v(-28.31, 8.14) * mm, "end": v(-28.47, 7.98) * mm});
            skLineSegment(sketch, "E483", {"start": v(-28.47, 7.98) * mm, "end": v(-28.63, 7.82) * mm});
            skLineSegment(sketch, "E484", {"start": v(-28.63, 7.82) * mm, "end": v(-29.03, 7.24) * mm});
            skLineSegment(sketch, "E485", {"start": v(-29.03, 7.24) * mm, "end": v(-29.3, 6.51) * mm});
            skLineSegment(sketch, "E486", {"start": v(-29.3, 6.51) * mm, "end": v(-29.38, 5.82) * mm});
            skLineSegment(sketch, "E487", {"start": v(-29.38, 5.82) * mm, "end": v(-29.39, 5.34) * mm});
            skLineSegment(sketch, "E488", {"start": v(-29.39, 5.34) * mm, "end": v(-29.39, 5.18) * mm});
            skLineSegment(sketch, "E489", {"start": v(-29.39, 5.18) * mm, "end": v(-29.39, 4.61) * mm});
            skLineSegment(sketch, "E490", {"start": v(-29.39, 4.61) * mm, "end": v(-29.39, 2.9) * mm});
            skLineSegment(sketch, "E491", {"start": v(-29.39, 2.9) * mm, "end": v(-29.39, -0.06) * mm});
            skLineSegment(sketch, "E492", {"start": v(-29.39, -0.06) * mm, "end": v(-29.39, -3.42) * mm});
            skLineSegment(sketch, "E493", {"start": v(-29.39, -3.42) * mm, "end": v(-29.39, -6.89) * mm});
            skLineSegment(sketch, "E494", {"start": v(-29.39, -6.89) * mm, "end": v(-29.39, -10.16) * mm});
            skLineSegment(sketch, "E495", {"start": v(-29.39, -10.16) * mm, "end": v(-29.39, -12.95) * mm});
            skLineSegment(sketch, "E496", {"start": v(-29.39, -12.95) * mm, "end": v(-29.39, -14.96) * mm});
            skLineSegment(sketch, "E497", {"start": v(-29.39, -14.96) * mm, "end": v(-29.39, -15.66) * mm});
            skLineSegment(sketch, "E498", {"start": v(-29.39, -15.66) * mm, "end": v(-29.39, -15.9) * mm});
            skLineSegment(sketch, "E499", {"start": v(-29.39, -15.9) * mm, "end": v(-28.69, -15.9) * mm});
            skLineSegment(sketch, "E500", {"start": v(-28.69, -15.9) * mm, "end": v(-27.12, -15.9) * mm});
            skLineSegment(sketch, "E501", {"start": v(-27.12, -15.9) * mm, "end": v(-26.6, -15.9) * mm});
            skLineSegment(sketch, "E502", {"start": v(-26.6, -15.9) * mm, "end": v(-26.6, -13.51) * mm});
            skLineSegment(sketch, "E503", {"start": v(-26.6, -13.51) * mm, "end": v(-26.6, -6.37) * mm});
            skLineSegment(sketch, "E504", {"start": v(-26.6, -6.37) * mm, "end": v(-26.6, 0.77) * mm});
            skLineSegment(sketch, "E505", {"start": v(-26.6, 0.77) * mm, "end": v(-26.6, 3.15) * mm});
            skLineSegment(sketch, "E506", {"start": v(-26.6, 3.15) * mm, "end": v(-26.6, 3.25) * mm});
            skLineSegment(sketch, "E507", {"start": v(-26.6, 3.25) * mm, "end": v(-26.48, 3.56) * mm});
            skLineSegment(sketch, "E508", {"start": v(-26.48, 3.56) * mm, "end": v(-26.17, 3.72) * mm});
            skLineSegment(sketch, "E509", {"start": v(-26.17, 3.72) * mm, "end": v(-26.07, 3.72) * mm});
            skLineSegment(sketch, "E510", {"start": v(-26.07, 3.72) * mm, "end": v(-25.96, 3.72) * mm});
            skLineSegment(sketch, "E511", {"start": v(-25.96, 3.72) * mm, "end": v(-25.66, 3.56) * mm});
            skLineSegment(sketch, "E512", {"start": v(-25.66, 3.56) * mm, "end": v(-25.53, 3.26) * mm});
            skLineSegment(sketch, "E513", {"start": v(-25.53, 3.26) * mm, "end": v(-25.53, 3.16) * mm});
            skLineSegment(sketch, "E514", {"start": v(-25.53, 3.16) * mm, "end": v(-25.53, 0.24) * mm});
            skLineSegment(sketch, "E515", {"start": v(-25.53, 0.24) * mm, "end": v(-25.53, -6.34) * mm});
            skLineSegment(sketch, "E516", {"start": v(-25.53, -6.34) * mm, "end": v(-25.53, -8.54) * mm});
            skLineSegment(sketch, "E517", {"start": v(-25.53, -8.54) * mm, "end": v(-25.53, -8.9) * mm});
            skLineSegment(sketch, "E518", {"start": v(-25.53, -8.9) * mm, "end": v(-25.48, -10) * mm});
            skLineSegment(sketch, "E519", {"start": v(-25.48, -10) * mm, "end": v(-25.24, -11.46) * mm});
            skLineSegment(sketch, "E520", {"start": v(-25.24, -11.46) * mm, "end": v(-24.7, -12.83) * mm});
            skLineSegment(sketch, "E521", {"start": v(-24.7, -12.83) * mm, "end": v(-23.99, -13.81) * mm});
            skLineSegment(sketch, "E522", {"start": v(-23.99, -13.81) * mm, "end": v(-23.7, -14.08) * mm});
            skLineSegment(sketch, "E523", {"start": v(-23.7, -14.08) * mm, "end": v(-23.43, -14.34) * mm});
            skLineSegment(sketch, "E524", {"start": v(-23.43, -14.34) * mm, "end": v(-22.57, -15.04) * mm});
            skLineSegment(sketch, "E525", {"start": v(-22.57, -15.04) * mm, "end": v(-21.52, -15.6) * mm});
            skLineSegment(sketch, "E526", {"start": v(-21.52, -15.6) * mm, "end": v(-20.26, -15.86) * mm});
            skLineSegment(sketch, "E527", {"start": v(-20.26, -15.86) * mm, "end": v(-18.96, -15.93) * mm});
            skLineSegment(sketch, "E528", {"start": v(-18.96, -15.93) * mm, "end": v(-18.52, -15.93) * mm});
            skLineSegment(sketch, "E529", {"start": v(-18.52, -15.93) * mm, "end": v(-18.09, -15.93) * mm});
            skLineSegment(sketch, "E530", {"start": v(-18.09, -15.93) * mm, "end": v(-16.78, -15.86) * mm});
            skLineSegment(sketch, "E531", {"start": v(-16.78, -15.86) * mm, "end": v(-15.52, -15.6) * mm});
            skLineSegment(sketch, "E532", {"start": v(-15.52, -15.6) * mm, "end": v(-14.47, -15.04) * mm});
            skLineSegment(sketch, "E533", {"start": v(-14.47, -15.04) * mm, "end": v(-13.61, -14.34) * mm});
            skLineSegment(sketch, "E534", {"start": v(-13.61, -14.34) * mm, "end": v(-13.35, -14.08) * mm});
            skLineSegment(sketch, "E535", {"start": v(-13.35, -14.08) * mm, "end": v(-13.06, -13.81) * mm});
            skLineSegment(sketch, "E536", {"start": v(-13.06, -13.81) * mm, "end": v(-12.34, -12.83) * mm});
            skLineSegment(sketch, "E537", {"start": v(-12.34, -12.83) * mm, "end": v(-11.75, -11.46) * mm});
            skLineSegment(sketch, "E538", {"start": v(-11.75, -11.46) * mm, "end": v(-11.47, -10) * mm});
            skLineSegment(sketch, "E539", {"start": v(-11.47, -10) * mm, "end": v(-11.4, -8.9) * mm});
            skLineSegment(sketch, "E540", {"start": v(-11.4, -8.9) * mm, "end": v(-11.4, -8.54) * mm});
            skLineSegment(sketch, "E541", {"start": v(-11.4, -8.54) * mm, "end": v(-11.4, -5.61) * mm});
            skLineSegment(sketch, "E542", {"start": v(-11.4, -5.61) * mm, "end": v(-11.4, 0.97) * mm});
            skLineSegment(sketch, "E543", {"start": v(-11.4, 0.97) * mm, "end": v(-11.4, 3.16) * mm});
            skLineSegment(sketch, "E544", {"start": v(-11.4, 3.16) * mm, "end": v(-11.4, 3.26) * mm});
            skLineSegment(sketch, "E545", {"start": v(-11.4, 3.26) * mm, "end": v(-11.25, 3.56) * mm});
            skLineSegment(sketch, "E546", {"start": v(-11.25, 3.56) * mm, "end": v(-10.92, 3.72) * mm});
            skLineSegment(sketch, "E547", {"start": v(-10.92, 3.72) * mm, "end": v(-10.8, 3.72) * mm});
            skLineSegment(sketch, "E548", {"start": v(-10.8, 3.72) * mm, "end": v(-10.7, 3.72) * mm});
            skLineSegment(sketch, "E549", {"start": v(-10.7, 3.72) * mm, "end": v(-10.37, 3.56) * mm});
            skLineSegment(sketch, "E550", {"start": v(-10.37, 3.56) * mm, "end": v(-10.22, 3.26) * mm});
            skLineSegment(sketch, "E551", {"start": v(-10.22, 3.26) * mm, "end": v(-10.22, 3.16) * mm});
            skLineSegment(sketch, "E552", {"start": v(-10.22, 3.16) * mm, "end": v(-10.22, 0.78) * mm});
            skLineSegment(sketch, "E553", {"start": v(-10.22, 0.78) * mm, "end": v(-10.22, -6.37) * mm});
            skLineSegment(sketch, "E554", {"start": v(-10.22, -6.37) * mm, "end": v(-10.22, -13.51) * mm});
            skLineSegment(sketch, "E555", {"start": v(-10.22, -13.51) * mm, "end": v(-10.22, -15.9) * mm});
            skLineSegment(sketch, "E556", {"start": v(-10.22, -15.9) * mm, "end": v(-9.57, -15.9) * mm});
            skLineSegment(sketch, "E557", {"start": v(-9.57, -15.9) * mm, "end": v(-8.1, -15.9) * mm});
            skLineSegment(sketch, "E558", {"start": v(-8.1, -15.9) * mm, "end": v(-7.61, -15.9) * mm});
            skLineSegment(sketch, "E559", {"start": v(-7.61, -15.9) * mm, "end": v(-7.61, -13.26) * mm});
            skLineSegment(sketch, "E560", {"start": v(-7.61, -13.26) * mm, "end": v(-7.61, -5.35) * mm});
            skLineSegment(sketch, "E561", {"start": v(-7.61, -5.35) * mm, "end": v(-7.61, 2.55) * mm});
            skLineSegment(sketch, "E562", {"start": v(-7.61, 2.55) * mm, "end": v(-7.61, 5.18) * mm});
            skLineSegment(sketch, "E563", {"start": v(-2.58, -5.15) * mm, "end": v(-2.58, -5.3) * mm});
            skLineSegment(sketch, "E564", {"start": v(-2.58, -5.3) * mm, "end": v(-2.59, -5.79) * mm});
            skLineSegment(sketch, "E565", {"start": v(-2.59, -5.79) * mm, "end": v(-2.52, -6.49) * mm});
            skLineSegment(sketch, "E566", {"start": v(-2.52, -6.49) * mm, "end": v(-2.26, -7.23) * mm});
            skLineSegment(sketch, "E567", {"start": v(-2.26, -7.23) * mm, "end": v(-1.87, -7.81) * mm});
            skLineSegment(sketch, "E568", {"start": v(-1.87, -7.81) * mm, "end": v(-1.7, -7.98) * mm});
            skLineSegment(sketch, "E569", {"start": v(-1.7, -7.98) * mm, "end": v(-1.55, -8.13) * mm});
            skLineSegment(sketch, "E570", {"start": v(-1.55, -8.13) * mm, "end": v(-1, -8.55) * mm});
            skLineSegment(sketch, "E571", {"start": v(-1, -8.55) * mm, "end": v(-0.38, -8.86) * mm});
            skLineSegment(sketch, "E572", {"start": v(-0.38, -8.86) * mm, "end": v(0.18, -8.98) * mm});
            skLineSegment(sketch, "E573", {"start": v(0.18, -8.98) * mm, "end": v(0.54, -9) * mm});
            skLineSegment(sketch, "E574", {"start": v(0.54, -9) * mm, "end": v(0.66, -9) * mm});
            skLineSegment(sketch, "E575", {"start": v(0.66, -9) * mm, "end": v(0.78, -9) * mm});
            skLineSegment(sketch, "E576", {"start": v(0.78, -9) * mm, "end": v(1.14, -8.98) * mm});
            skLineSegment(sketch, "E577", {"start": v(1.14, -8.98) * mm, "end": v(1.7, -8.86) * mm});
            skLineSegment(sketch, "E578", {"start": v(1.7, -8.86) * mm, "end": v(2.33, -8.55) * mm});
            skLineSegment(sketch, "E579", {"start": v(2.33, -8.55) * mm, "end": v(2.87, -8.13) * mm});
            skLineSegment(sketch, "E580", {"start": v(2.87, -8.13) * mm, "end": v(3.03, -7.98) * mm});
            skLineSegment(sketch, "E581", {"start": v(3.03, -7.98) * mm, "end": v(3.2, -7.81) * mm});
            skLineSegment(sketch, "E582", {"start": v(3.2, -7.81) * mm, "end": v(3.59, -7.23) * mm});
            skLineSegment(sketch, "E583", {"start": v(3.59, -7.23) * mm, "end": v(3.84, -6.49) * mm});
            skLineSegment(sketch, "E584", {"start": v(3.84, -6.49) * mm, "end": v(3.91, -5.79) * mm});
            skLineSegment(sketch, "E585", {"start": v(3.91, -5.79) * mm, "end": v(3.91, -5.3) * mm});
            skLineSegment(sketch, "E586", {"start": v(3.91, -5.3) * mm, "end": v(3.91, -5.15) * mm});
            skLineSegment(sketch, "E587", {"start": v(3.91, -5.15) * mm, "end": v(3.91, -4.6) * mm});
            skLineSegment(sketch, "E588", {"start": v(3.91, -4.6) * mm, "end": v(3.91, -2.95) * mm});
            skLineSegment(sketch, "E589", {"start": v(3.91, -2.95) * mm, "end": v(3.91, -0.04) * mm});
            skLineSegment(sketch, "E590", {"start": v(3.91, -0.04) * mm, "end": v(3.91, 3.3) * mm});
            skLineSegment(sketch, "E591", {"start": v(3.91, 3.3) * mm, "end": v(3.91, 6.76) * mm});
            skLineSegment(sketch, "E592", {"start": v(3.91, 6.76) * mm, "end": v(3.91, 10.04) * mm});
            skLineSegment(sketch, "E593", {"start": v(3.91, 10.04) * mm, "end": v(3.91, 12.85) * mm});
            skLineSegment(sketch, "E594", {"start": v(3.91, 12.85) * mm, "end": v(3.91, 14.87) * mm});
            skLineSegment(sketch, "E595", {"start": v(3.91, 14.87) * mm, "end": v(3.91, 15.58) * mm});
            skLineSegment(sketch, "E596", {"start": v(3.91, 15.58) * mm, "end": v(3.91, 15.82) * mm});
            skLineSegment(sketch, "E597", {"start": v(3.91, 15.82) * mm, "end": v(3.24, 15.82) * mm});
            skLineSegment(sketch, "E598", {"start": v(3.24, 15.82) * mm, "end": v(1.73, 15.82) * mm});
            skLineSegment(sketch, "E599", {"start": v(1.73, 15.82) * mm, "end": v(1.22, 15.82) * mm});
            skLineSegment(sketch, "E600", {"start": v(1.22, 15.82) * mm, "end": v(1.22, 13.45) * mm});
            skLineSegment(sketch, "E601", {"start": v(1.22, 13.45) * mm, "end": v(1.22, 6.35) * mm});
            skLineSegment(sketch, "E602", {"start": v(1.22, 6.35) * mm, "end": v(1.22, -0.76) * mm});
            skLineSegment(sketch, "E603", {"start": v(1.22, -0.76) * mm, "end": v(1.22, -3.12) * mm});
            skLineSegment(sketch, "E604", {"start": v(1.22, -3.12) * mm, "end": v(1.22, -3.23) * mm});
            skLineSegment(sketch, "E605", {"start": v(1.22, -3.23) * mm, "end": v(1.09, -3.54) * mm});
            skLineSegment(sketch, "E606", {"start": v(1.09, -3.54) * mm, "end": v(0.77, -3.71) * mm});
            skLineSegment(sketch, "E607", {"start": v(0.77, -3.71) * mm, "end": v(0.66, -3.71) * mm});
            skLineSegment(sketch, "E608", {"start": v(0.66, -3.71) * mm, "end": v(0.55, -3.71) * mm});
            skLineSegment(sketch, "E609", {"start": v(0.55, -3.71) * mm, "end": v(0.22, -3.54) * mm});
            skLineSegment(sketch, "E610", {"start": v(0.22, -3.54) * mm, "end": v(0.08, -3.23) * mm});
            skLineSegment(sketch, "E611", {"start": v(0.08, -3.23) * mm, "end": v(0.08, -3.12) * mm});
            skLineSegment(sketch, "E612", {"start": v(0.08, -3.12) * mm, "end": v(0.08, -0.76) * mm});
            skLineSegment(sketch, "E613", {"start": v(0.08, -0.76) * mm, "end": v(0.08, 6.35) * mm});
            skLineSegment(sketch, "E614", {"start": v(0.08, 6.35) * mm, "end": v(0.08, 13.45) * mm});
            skLineSegment(sketch, "E615", {"start": v(0.08, 13.45) * mm, "end": v(0.08, 15.82) * mm});
            skLineSegment(sketch, "E616", {"start": v(0.08, 15.82) * mm, "end": v(-0.59, 15.82) * mm});
            skLineSegment(sketch, "E617", {"start": v(-0.59, 15.82) * mm, "end": v(-2.08, 15.82) * mm});
            skLineSegment(sketch, "E618", {"start": v(-2.08, 15.82) * mm, "end": v(-2.58, 15.82) * mm});
            skLineSegment(sketch, "E619", {"start": v(-2.58, 15.82) * mm, "end": v(-2.58, 10.58) * mm});
            skLineSegment(sketch, "E620", {"start": v(-2.58, 10.58) * mm, "end": v(-2.58, -1.22) * mm});
            skLineSegment(sketch, "E621", {"start": v(-2.58, -1.22) * mm, "end": v(-2.58, -5.15) * mm});
            skLineSegment(sketch, "E622", {"start": v(27.9, -15.94) * mm, "end": v(33.07, -15.93) * mm});
            skLineSegment(sketch, "E623", {"start": v(33.07, -15.93) * mm, "end": v(33.06, 15.82) * mm});
            skLineSegment(sketch, "E624", {"start": v(33.06, 15.82) * mm, "end": v(27.9, 15.82) * mm});
            skLineSegment(sketch, "E625", {"start": v(27.9, 15.82) * mm, "end": v(27.9, -15.94) * mm});
            skSolve(sketch);
        }
        {
            var Q0;
            Q0 = qSketchRegion(id + "F2", true);
            extrude(context, id + "F3", {"entities" : qUnion([Q0]), "depth" : 5 * mm, "offsetDistance" : 25 * mm});
        }
        {
            var Q0;
            Q0=makeQuery(id+"F3.opExtrude","SWEPT_BODY",BODY,{"disambiguationData":[OSD([sQuery(id+"F2.wireOp",EDGE,"E1"),sQuery(id+"F2.wireOp",EDGE,"E2"),sQuery(id+"F2.wireOp",EDGE,"E3"),sQuery(id+"F2.wireOp",EDGE,"E4"),sQuery(id+"F2.wireOp",EDGE,"E5"),sQuery(id+"F2.wireOp",EDGE,"E6"),sQuery(id+"F2.wireOp",EDGE,"E7"),sQuery(id+"F2.wireOp",EDGE,"E8"),sQuery(id+"F2.wireOp",EDGE,"E9"),sQuery(id+"F2.wireOp",EDGE,"E10"),sQuery(id+"F2.wireOp",EDGE,"E11"),sQuery(id+"F2.wireOp",EDGE,"E12"),sQuery(id+"F2.wireOp",EDGE,"E13"),sQuery(id+"F2.wireOp",EDGE,"E14"),sQuery(id+"F2.wireOp",EDGE,"E15"),sQuery(id+"F2.wireOp",EDGE,"E16"),sQuery(id+"F2.wireOp",EDGE,"E17"),sQuery(id+"F2.wireOp",EDGE,"E18"),sQuery(id+"F2.wireOp",EDGE,"E19"),sQuery(id+"F2.wireOp",EDGE,"E20"),sQuery(id+"F2.wireOp",EDGE,"E21"),sQuery(id+"F2.wireOp",EDGE,"E22"),sQuery(id+"F2.wireOp",EDGE,"E23"),sQuery(id+"F2.wireOp",EDGE,"E24"),sQuery(id+"F2.wireOp",EDGE,"E25"),sQuery(id+"F2.wireOp",EDGE,"E26"),sQuery(id+"F2.wireOp",EDGE,"E27"),sQuery(id+"F2.wireOp",EDGE,"E28"),sQuery(id+"F2.wireOp",EDGE,"E29"),sQuery(id+"F2.wireOp",EDGE,"E30"),sQuery(id+"F2.wireOp",EDGE,"E31"),sQuery(id+"F2.wireOp",EDGE,"E32"),sQuery(id+"F2.wireOp",EDGE,"E33"),sQuery(id+"F2.wireOp",EDGE,"E34"),sQuery(id+"F2.wireOp",EDGE,"E35"),sQuery(id+"F2.wireOp",EDGE,"E36"),sQuery(id+"F2.wireOp",EDGE,"E37"),sQuery(id+"F2.wireOp",EDGE,"E38"),sQuery(id+"F2.wireOp",EDGE,"E39"),sQuery(id+"F2.wireOp",EDGE,"E40"),sQuery(id+"F2.wireOp",EDGE,"E41"),sQuery(id+"F2.wireOp",EDGE,"E42"),sQuery(id+"F2.wireOp",EDGE,"E43"),sQuery(id+"F2.wireOp",EDGE,"E44"),sQuery(id+"F2.wireOp",EDGE,"E45"),sQuery(id+"F2.wireOp",EDGE,"E46"),sQuery(id+"F2.wireOp",EDGE,"E47"),sQuery(id+"F2.wireOp",EDGE,"E48"),sQuery(id+"F2.wireOp",EDGE,"E49"),sQuery(id+"F2.wireOp",EDGE,"E50"),sQuery(id+"F2.wireOp",EDGE,"E51"),sQuery(id+"F2.wireOp",EDGE,"E52"),sQuery(id+"F2.wireOp",EDGE,"E53"),sQuery(id+"F2.wireOp",EDGE,"E54"),sQuery(id+"F2.wireOp",EDGE,"E55"),sQuery(id+"F2.wireOp",EDGE,"E56"),sQuery(id+"F2.wireOp",EDGE,"E57"),sQuery(id+"F2.wireOp",EDGE,"E58"),sQuery(id+"F2.wireOp",EDGE,"E59"),sQuery(id+"F2.wireOp",EDGE,"E60"),sQuery(id+"F2.wireOp",EDGE,"E61"),sQuery(id+"F2.wireOp",EDGE,"E62"),sQuery(id+"F2.wireOp",EDGE,"E63"),sQuery(id+"F2.wireOp",EDGE,"E64"),sQuery(id+"F2.wireOp",EDGE,"E65"),sQuery(id+"F2.wireOp",EDGE,"E66"),sQuery(id+"F2.wireOp",EDGE,"E67"),sQuery(id+"F2.wireOp",EDGE,"E68"),sQuery(id+"F2.wireOp",EDGE,"E69"),sQuery(id+"F2.wireOp",EDGE,"E70"),sQuery(id+"F2.wireOp",EDGE,"E71"),sQuery(id+"F2.wireOp",EDGE,"E72"),sQuery(id+"F2.wireOp",EDGE,"E73"),sQuery(id+"F2.wireOp",EDGE,"E74"),sQuery(id+"F2.wireOp",EDGE,"E75"),sQuery(id+"F2.wireOp",EDGE,"E76"),sQuery(id+"F2.wireOp",EDGE,"E77"),sQuery(id+"F2.wireOp",EDGE,"E78"),sQuery(id+"F2.wireOp",EDGE,"E79"),sQuery(id+"F2.wireOp",EDGE,"E80"),sQuery(id+"F2.wireOp",EDGE,"E81"),sQuery(id+"F2.wireOp",EDGE,"E82"),sQuery(id+"F2.wireOp",EDGE,"E83"),sQuery(id+"F2.wireOp",EDGE,"E84"),sQuery(id+"F2.wireOp",EDGE,"E85"),sQuery(id+"F2.wireOp",EDGE,"E86"),sQuery(id+"F2.wireOp",EDGE,"E87"),sQuery(id+"F2.wireOp",EDGE,"E88"),sQuery(id+"F2.wireOp",EDGE,"E89"),sQuery(id+"F2.wireOp",EDGE,"E90"),sQuery(id+"F2.wireOp",EDGE,"E91"),sQuery(id+"F2.wireOp",EDGE,"E92"),sQuery(id+"F2.wireOp",EDGE,"E93"),sQuery(id+"F2.wireOp",EDGE,"E94"),sQuery(id+"F2.wireOp",EDGE,"E95"),sQuery(id+"F2.wireOp",EDGE,"E96"),sQuery(id+"F2.wireOp",EDGE,"E97"),sQuery(id+"F2.wireOp",EDGE,"E98"),sQuery(id+"F2.wireOp",EDGE,"E99"),sQuery(id+"F2.wireOp",EDGE,"E100"),sQuery(id+"F2.wireOp",EDGE,"E101"),sQuery(id+"F2.wireOp",EDGE,"E102"),sQuery(id+"F2.wireOp",EDGE,"E103"),sQuery(id+"F2.wireOp",EDGE,"E104"),sQuery(id+"F2.wireOp",EDGE,"E105"),sQuery(id+"F2.wireOp",EDGE,"E106"),sQuery(id+"F2.wireOp",EDGE,"E107"),sQuery(id+"F2.wireOp",EDGE,"E108"),sQuery(id+"F2.wireOp",EDGE,"E109"),sQuery(id+"F2.wireOp",EDGE,"E110"),sQuery(id+"F2.wireOp",EDGE,"E111"),sQuery(id+"F2.wireOp",EDGE,"E112"),sQuery(id+"F2.wireOp",EDGE,"E113"),sQuery(id+"F2.wireOp",EDGE,"E114"),sQuery(id+"F2.wireOp",EDGE,"E115"),sQuery(id+"F2.wireOp",EDGE,"E116"),sQuery(id+"F2.wireOp",EDGE,"E117"),sQuery(id+"F2.wireOp",EDGE,"E118"),sQuery(id+"F2.wireOp",EDGE,"E119"),sQuery(id+"F2.wireOp",EDGE,"E120"),sQuery(id+"F2.wireOp",EDGE,"E121"),sQuery(id+"F2.wireOp",EDGE,"E122"),sQuery(id+"F2.wireOp",EDGE,"E123"),sQuery(id+"F2.wireOp",EDGE,"E124"),sQuery(id+"F2.wireOp",EDGE,"E125"),sQuery(id+"F2.wireOp",EDGE,"E126"),sQuery(id+"F2.wireOp",EDGE,"E127"),sQuery(id+"F2.wireOp",EDGE,"E128"),sQuery(id+"F2.wireOp",EDGE,"E129"),sQuery(id+"F2.wireOp",EDGE,"E130"),sQuery(id+"F2.wireOp",EDGE,"E131"),sQuery(id+"F2.wireOp",EDGE,"E132"),sQuery(id+"F2.wireOp",EDGE,"E133"),sQuery(id+"F2.wireOp",EDGE,"E134"),sQuery(id+"F2.wireOp",EDGE,"E135"),sQuery(id+"F2.wireOp",EDGE,"E136"),sQuery(id+"F2.wireOp",EDGE,"E137"),sQuery(id+"F2.wireOp",EDGE,"E138"),sQuery(id+"F2.wireOp",EDGE,"E139"),sQuery(id+"F2.wireOp",EDGE,"E140"),sQuery(id+"F2.wireOp",EDGE,"E141"),sQuery(id+"F2.wireOp",EDGE,"E142"),sQuery(id+"F2.wireOp",EDGE,"E143"),sQuery(id+"F2.wireOp",EDGE,"E144"),sQuery(id+"F2.wireOp",EDGE,"E145"),sQuery(id+"F2.wireOp",EDGE,"E146"),sQuery(id+"F2.wireOp",EDGE,"E147"),sQuery(id+"F2.wireOp",EDGE,"E148"),sQuery(id+"F2.wireOp",EDGE,"E149"),sQuery(id+"F2.wireOp",EDGE,"E150"),sQuery(id+"F2.wireOp",EDGE,"E151"),sQuery(id+"F2.wireOp",EDGE,"E152"),sQuery(id+"F2.wireOp",EDGE,"E153"),sQuery(id+"F2.wireOp",EDGE,"E154"),sQuery(id+"F2.wireOp",EDGE,"E155"),sQuery(id+"F2.wireOp",EDGE,"E156"),sQuery(id+"F2.wireOp",EDGE,"E157"),sQuery(id+"F2.wireOp",EDGE,"E158"),sQuery(id+"F2.wireOp",EDGE,"E159"),sQuery(id+"F2.wireOp",EDGE,"E160"),sQuery(id+"F2.wireOp",EDGE,"E161"),sQuery(id+"F2.wireOp",EDGE,"E162"),sQuery(id+"F2.wireOp",EDGE,"E163"),sQuery(id+"F2.wireOp",EDGE,"E164"),sQuery(id+"F2.wireOp",EDGE,"E165"),sQuery(id+"F2.wireOp",EDGE,"E166"),sQuery(id+"F2.wireOp",EDGE,"E167"),sQuery(id+"F2.wireOp",EDGE,"E168"),sQuery(id+"F2.wireOp",EDGE,"E169"),sQuery(id+"F2.wireOp",EDGE,"E170"),sQuery(id+"F2.wireOp",EDGE,"E171"),sQuery(id+"F2.wireOp",EDGE,"E172"),sQuery(id+"F2.wireOp",EDGE,"E173"),sQuery(id+"F2.wireOp",EDGE,"E174"),sQuery(id+"F2.wireOp",EDGE,"E175"),sQuery(id+"F2.wireOp",EDGE,"E176"),sQuery(id+"F2.wireOp",EDGE,"E177"),sQuery(id+"F2.wireOp",EDGE,"E178"),sQuery(id+"F2.wireOp",EDGE,"E179"),sQuery(id+"F2.wireOp",EDGE,"E180"),sQuery(id+"F2.wireOp",EDGE,"E181"),sQuery(id+"F2.wireOp",EDGE,"E182"),sQuery(id+"F2.wireOp",EDGE,"E183"),sQuery(id+"F2.wireOp",EDGE,"E184"),sQuery(id+"F2.wireOp",EDGE,"E185"),sQuery(id+"F2.wireOp",EDGE,"E186"),sQuery(id+"F2.wireOp",EDGE,"E187"),sQuery(id+"F2.wireOp",EDGE,"E188"),sQuery(id+"F2.wireOp",EDGE,"E189"),sQuery(id+"F2.wireOp",EDGE,"E190"),sQuery(id+"F2.wireOp",EDGE,"E191"),sQuery(id+"F2.wireOp",EDGE,"E192"),sQuery(id+"F2.wireOp",EDGE,"E193"),sQuery(id+"F2.wireOp",EDGE,"E194"),sQuery(id+"F2.wireOp",EDGE,"E195"),sQuery(id+"F2.wireOp",EDGE,"E196"),sQuery(id+"F2.wireOp",EDGE,"E197"),sQuery(id+"F2.wireOp",EDGE,"E198"),sQuery(id+"F2.wireOp",EDGE,"E199"),sQuery(id+"F2.wireOp",EDGE,"E200"),sQuery(id+"F2.wireOp",EDGE,"E201"),sQuery(id+"F2.wireOp",EDGE,"E202"),sQuery(id+"F2.wireOp",EDGE,"E203"),sQuery(id+"F2.wireOp",EDGE,"E204"),sQuery(id+"F2.wireOp",EDGE,"E205"),sQuery(id+"F2.wireOp",EDGE,"E206"),sQuery(id+"F2.wireOp",EDGE,"E207"),sQuery(id+"F2.wireOp",EDGE,"E208"),sQuery(id+"F2.wireOp",EDGE,"E209"),sQuery(id+"F2.wireOp",EDGE,"E210"),sQuery(id+"F2.wireOp",EDGE,"E211"),sQuery(id+"F2.wireOp",EDGE,"E212"),sQuery(id+"F2.wireOp",EDGE,"E213"),sQuery(id+"F2.wireOp",EDGE,"E214"),sQuery(id+"F2.wireOp",EDGE,"E215"),sQuery(id+"F2.wireOp",EDGE,"E216"),sQuery(id+"F2.wireOp",EDGE,"E217"),sQuery(id+"F2.wireOp",EDGE,"E218"),sQuery(id+"F2.wireOp",EDGE,"E219"),sQuery(id+"F2.wireOp",EDGE,"E220"),sQuery(id+"F2.wireOp",EDGE,"E221"),sQuery(id+"F2.wireOp",EDGE,"E222"),sQuery(id+"F2.wireOp",EDGE,"E223"),sQuery(id+"F2.wireOp",EDGE,"E224"),sQuery(id+"F2.wireOp",EDGE,"E225"),sQuery(id+"F2.wireOp",EDGE,"E226"),sQuery(id+"F2.wireOp",EDGE,"E227"),sQuery(id+"F2.wireOp",EDGE,"E228"),sQuery(id+"F2.wireOp",EDGE,"E229"),sQuery(id+"F2.wireOp",EDGE,"E230"),sQuery(id+"F2.wireOp",EDGE,"E231"),sQuery(id+"F2.wireOp",EDGE,"E232"),sQuery(id+"F2.wireOp",EDGE,"E233"),sQuery(id+"F2.wireOp",EDGE,"E234"),sQuery(id+"F2.wireOp",EDGE,"E235"),sQuery(id+"F2.wireOp",EDGE,"E236"),sQuery(id+"F2.wireOp",EDGE,"E237"),sQuery(id+"F2.wireOp",EDGE,"E238"),sQuery(id+"F2.wireOp",EDGE,"E239"),sQuery(id+"F2.wireOp",EDGE,"E240"),sQuery(id+"F2.wireOp",EDGE,"E241"),sQuery(id+"F2.wireOp",EDGE,"E242"),sQuery(id+"F2.wireOp",EDGE,"E243"),sQuery(id+"F2.wireOp",EDGE,"E244"),sQuery(id+"F2.wireOp",EDGE,"E245"),sQuery(id+"F2.wireOp",EDGE,"E246"),sQuery(id+"F2.wireOp",EDGE,"E247"),sQuery(id+"F2.wireOp",EDGE,"E248"),sQuery(id+"F2.wireOp",EDGE,"E249"),sQuery(id+"F2.wireOp",EDGE,"E250"),sQuery(id+"F2.wireOp",EDGE,"E251"),sQuery(id+"F2.wireOp",EDGE,"E252"),sQuery(id+"F2.wireOp",EDGE,"E253"),sQuery(id+"F2.wireOp",EDGE,"E254"),sQuery(id+"F2.wireOp",EDGE,"E255"),sQuery(id+"F2.wireOp",EDGE,"E256"),sQuery(id+"F2.wireOp",EDGE,"E257"),sQuery(id+"F2.wireOp",EDGE,"E258"),sQuery(id+"F2.wireOp",EDGE,"E259"),sQuery(id+"F2.wireOp",EDGE,"E260"),sQuery(id+"F2.wireOp",EDGE,"E261"),sQuery(id+"F2.wireOp",EDGE,"E262"),sQuery(id+"F2.wireOp",EDGE,"E263"),sQuery(id+"F2.wireOp",EDGE,"E264"),sQuery(id+"F2.wireOp",EDGE,"E265"),sQuery(id+"F2.wireOp",EDGE,"E266"),sQuery(id+"F2.wireOp",EDGE,"E267"),sQuery(id+"F2.wireOp",EDGE,"E268"),sQuery(id+"F2.wireOp",EDGE,"E269"),sQuery(id+"F2.wireOp",EDGE,"E270"),sQuery(id+"F2.wireOp",EDGE,"E271"),sQuery(id+"F2.wireOp",EDGE,"E272"),sQuery(id+"F2.wireOp",EDGE,"E273"),sQuery(id+"F2.wireOp",EDGE,"E274"),sQuery(id+"F2.wireOp",EDGE,"E275"),sQuery(id+"F2.wireOp",EDGE,"E276"),sQuery(id+"F2.wireOp",EDGE,"E277"),sQuery(id+"F2.wireOp",EDGE,"E278"),sQuery(id+"F2.wireOp",EDGE,"E279"),sQuery(id+"F2.wireOp",EDGE,"E280"),sQuery(id+"F2.wireOp",EDGE,"E281"),sQuery(id+"F2.wireOp",EDGE,"E282"),sQuery(id+"F2.wireOp",EDGE,"E283"),sQuery(id+"F2.wireOp",EDGE,"E284"),sQuery(id+"F2.wireOp",EDGE,"E285"),sQuery(id+"F2.wireOp",EDGE,"E286"),sQuery(id+"F2.wireOp",EDGE,"E287"),sQuery(id+"F2.wireOp",EDGE,"E288"),sQuery(id+"F2.wireOp",EDGE,"E289"),sQuery(id+"F2.wireOp",EDGE,"E290"),sQuery(id+"F2.wireOp",EDGE,"E291"),sQuery(id+"F2.wireOp",EDGE,"E292"),sQuery(id+"F2.wireOp",EDGE,"E293"),sQuery(id+"F2.wireOp",EDGE,"E294"),sQuery(id+"F2.wireOp",EDGE,"E295"),sQuery(id+"F2.wireOp",EDGE,"E296"),sQuery(id+"F2.wireOp",EDGE,"E297"),sQuery(id+"F2.wireOp",EDGE,"E298"),sQuery(id+"F2.wireOp",EDGE,"E299"),sQuery(id+"F2.wireOp",EDGE,"E300"),sQuery(id+"F2.wireOp",EDGE,"E301")])]});
            var Q1;
            Q1=makeQuery(id+"F3.opExtrude","SWEPT_BODY",BODY,{"disambiguationData":[OSD([sQuery(id+"F2.wireOp",EDGE,"E302"),sQuery(id+"F2.wireOp",EDGE,"E303"),sQuery(id+"F2.wireOp",EDGE,"E304"),sQuery(id+"F2.wireOp",EDGE,"E305"),sQuery(id+"F2.wireOp",EDGE,"E306"),sQuery(id+"F2.wireOp",EDGE,"E307"),sQuery(id+"F2.wireOp",EDGE,"E308"),sQuery(id+"F2.wireOp",EDGE,"E309"),sQuery(id+"F2.wireOp",EDGE,"E310"),sQuery(id+"F2.wireOp",EDGE,"E311"),sQuery(id+"F2.wireOp",EDGE,"E312"),sQuery(id+"F2.wireOp",EDGE,"E313"),sQuery(id+"F2.wireOp",EDGE,"E314"),sQuery(id+"F2.wireOp",EDGE,"E315"),sQuery(id+"F2.wireOp",EDGE,"E316"),sQuery(id+"F2.wireOp",EDGE,"E317"),sQuery(id+"F2.wireOp",EDGE,"E318"),sQuery(id+"F2.wireOp",EDGE,"E319"),sQuery(id+"F2.wireOp",EDGE,"E320"),sQuery(id+"F2.wireOp",EDGE,"E321"),sQuery(id+"F2.wireOp",EDGE,"E322"),sQuery(id+"F2.wireOp",EDGE,"E323"),sQuery(id+"F2.wireOp",EDGE,"E324"),sQuery(id+"F2.wireOp",EDGE,"E325"),sQuery(id+"F2.wireOp",EDGE,"E326"),sQuery(id+"F2.wireOp",EDGE,"E327"),sQuery(id+"F2.wireOp",EDGE,"E328"),sQuery(id+"F2.wireOp",EDGE,"E329"),sQuery(id+"F2.wireOp",EDGE,"E330"),sQuery(id+"F2.wireOp",EDGE,"E331"),sQuery(id+"F2.wireOp",EDGE,"E332"),sQuery(id+"F2.wireOp",EDGE,"E333"),sQuery(id+"F2.wireOp",EDGE,"E334"),sQuery(id+"F2.wireOp",EDGE,"E335"),sQuery(id+"F2.wireOp",EDGE,"E336"),sQuery(id+"F2.wireOp",EDGE,"E337"),sQuery(id+"F2.wireOp",EDGE,"E338"),sQuery(id+"F2.wireOp",EDGE,"E339"),sQuery(id+"F2.wireOp",EDGE,"E340"),sQuery(id+"F2.wireOp",EDGE,"E341"),sQuery(id+"F2.wireOp",EDGE,"E342"),sQuery(id+"F2.wireOp",EDGE,"E343"),sQuery(id+"F2.wireOp",EDGE,"E344"),sQuery(id+"F2.wireOp",EDGE,"E345"),sQuery(id+"F2.wireOp",EDGE,"E346"),sQuery(id+"F2.wireOp",EDGE,"E347"),sQuery(id+"F2.wireOp",EDGE,"E348"),sQuery(id+"F2.wireOp",EDGE,"E349"),sQuery(id+"F2.wireOp",EDGE,"E350"),sQuery(id+"F2.wireOp",EDGE,"E351"),sQuery(id+"F2.wireOp",EDGE,"E352"),sQuery(id+"F2.wireOp",EDGE,"E353"),sQuery(id+"F2.wireOp",EDGE,"E354"),sQuery(id+"F2.wireOp",EDGE,"E355"),sQuery(id+"F2.wireOp",EDGE,"E356"),sQuery(id+"F2.wireOp",EDGE,"E357"),sQuery(id+"F2.wireOp",EDGE,"E358"),sQuery(id+"F2.wireOp",EDGE,"E359"),sQuery(id+"F2.wireOp",EDGE,"E360"),sQuery(id+"F2.wireOp",EDGE,"E361"),sQuery(id+"F2.wireOp",EDGE,"E362"),sQuery(id+"F2.wireOp",EDGE,"E363"),sQuery(id+"F2.wireOp",EDGE,"E364"),sQuery(id+"F2.wireOp",EDGE,"E365"),sQuery(id+"F2.wireOp",EDGE,"E366"),sQuery(id+"F2.wireOp",EDGE,"E367"),sQuery(id+"F2.wireOp",EDGE,"E368"),sQuery(id+"F2.wireOp",EDGE,"E369"),sQuery(id+"F2.wireOp",EDGE,"E370"),sQuery(id+"F2.wireOp",EDGE,"E371"),sQuery(id+"F2.wireOp",EDGE,"E372"),sQuery(id+"F2.wireOp",EDGE,"E373"),sQuery(id+"F2.wireOp",EDGE,"E374"),sQuery(id+"F2.wireOp",EDGE,"E375"),sQuery(id+"F2.wireOp",EDGE,"E376"),sQuery(id+"F2.wireOp",EDGE,"E377"),sQuery(id+"F2.wireOp",EDGE,"E378"),sQuery(id+"F2.wireOp",EDGE,"E379"),sQuery(id+"F2.wireOp",EDGE,"E380"),sQuery(id+"F2.wireOp",EDGE,"E381"),sQuery(id+"F2.wireOp",EDGE,"E382"),sQuery(id+"F2.wireOp",EDGE,"E383"),sQuery(id+"F2.wireOp",EDGE,"E384"),sQuery(id+"F2.wireOp",EDGE,"E385"),sQuery(id+"F2.wireOp",EDGE,"E386"),sQuery(id+"F2.wireOp",EDGE,"E387"),sQuery(id+"F2.wireOp",EDGE,"E388"),sQuery(id+"F2.wireOp",EDGE,"E389"),sQuery(id+"F2.wireOp",EDGE,"E390"),sQuery(id+"F2.wireOp",EDGE,"E391"),sQuery(id+"F2.wireOp",EDGE,"E392"),sQuery(id+"F2.wireOp",EDGE,"E393"),sQuery(id+"F2.wireOp",EDGE,"E394"),sQuery(id+"F2.wireOp",EDGE,"E395"),sQuery(id+"F2.wireOp",EDGE,"E396"),sQuery(id+"F2.wireOp",EDGE,"E397"),sQuery(id+"F2.wireOp",EDGE,"E398"),sQuery(id+"F2.wireOp",EDGE,"E399"),sQuery(id+"F2.wireOp",EDGE,"E400"),sQuery(id+"F2.wireOp",EDGE,"E401"),sQuery(id+"F2.wireOp",EDGE,"E402"),sQuery(id+"F2.wireOp",EDGE,"E403"),sQuery(id+"F2.wireOp",EDGE,"E404"),sQuery(id+"F2.wireOp",EDGE,"E405"),sQuery(id+"F2.wireOp",EDGE,"E406"),sQuery(id+"F2.wireOp",EDGE,"E407"),sQuery(id+"F2.wireOp",EDGE,"E408"),sQuery(id+"F2.wireOp",EDGE,"E409"),sQuery(id+"F2.wireOp",EDGE,"E410"),sQuery(id+"F2.wireOp",EDGE,"E411"),sQuery(id+"F2.wireOp",EDGE,"E412"),sQuery(id+"F2.wireOp",EDGE,"E413")])]});
            var Q2;
            Q2=makeQuery(id+"F3.opExtrude","SWEPT_BODY",BODY,{"disambiguationData":[OSD([sQuery(id+"F2.wireOp",EDGE,"E414"),sQuery(id+"F2.wireOp",EDGE,"E415"),sQuery(id+"F2.wireOp",EDGE,"E416"),sQuery(id+"F2.wireOp",EDGE,"E417"),sQuery(id+"F2.wireOp",EDGE,"E418"),sQuery(id+"F2.wireOp",EDGE,"E419"),sQuery(id+"F2.wireOp",EDGE,"E420"),sQuery(id+"F2.wireOp",EDGE,"E421"),sQuery(id+"F2.wireOp",EDGE,"E422"),sQuery(id+"F2.wireOp",EDGE,"E423"),sQuery(id+"F2.wireOp",EDGE,"E424"),sQuery(id+"F2.wireOp",EDGE,"E425"),sQuery(id+"F2.wireOp",EDGE,"E426"),sQuery(id+"F2.wireOp",EDGE,"E427"),sQuery(id+"F2.wireOp",EDGE,"E428"),sQuery(id+"F2.wireOp",EDGE,"E429"),sQuery(id+"F2.wireOp",EDGE,"E430"),sQuery(id+"F2.wireOp",EDGE,"E431"),sQuery(id+"F2.wireOp",EDGE,"E432"),sQuery(id+"F2.wireOp",EDGE,"E433"),sQuery(id+"F2.wireOp",EDGE,"E434"),sQuery(id+"F2.wireOp",EDGE,"E435"),sQuery(id+"F2.wireOp",EDGE,"E436"),sQuery(id+"F2.wireOp",EDGE,"E437"),sQuery(id+"F2.wireOp",EDGE,"E438"),sQuery(id+"F2.wireOp",EDGE,"E439"),sQuery(id+"F2.wireOp",EDGE,"E440"),sQuery(id+"F2.wireOp",EDGE,"E441"),sQuery(id+"F2.wireOp",EDGE,"E442"),sQuery(id+"F2.wireOp",EDGE,"E443"),sQuery(id+"F2.wireOp",EDGE,"E444"),sQuery(id+"F2.wireOp",EDGE,"E445"),sQuery(id+"F2.wireOp",EDGE,"E446"),sQuery(id+"F2.wireOp",EDGE,"E447"),sQuery(id+"F2.wireOp",EDGE,"E448"),sQuery(id+"F2.wireOp",EDGE,"E449"),sQuery(id+"F2.wireOp",EDGE,"E450"),sQuery(id+"F2.wireOp",EDGE,"E451"),sQuery(id+"F2.wireOp",EDGE,"E452"),sQuery(id+"F2.wireOp",EDGE,"E453"),sQuery(id+"F2.wireOp",EDGE,"E454"),sQuery(id+"F2.wireOp",EDGE,"E455"),sQuery(id+"F2.wireOp",EDGE,"E456"),sQuery(id+"F2.wireOp",EDGE,"E457"),sQuery(id+"F2.wireOp",EDGE,"E458"),sQuery(id+"F2.wireOp",EDGE,"E459"),sQuery(id+"F2.wireOp",EDGE,"E460"),sQuery(id+"F2.wireOp",EDGE,"E461"),sQuery(id+"F2.wireOp",EDGE,"E462"),sQuery(id+"F2.wireOp",EDGE,"E463"),sQuery(id+"F2.wireOp",EDGE,"E464"),sQuery(id+"F2.wireOp",EDGE,"E465"),sQuery(id+"F2.wireOp",EDGE,"E466"),sQuery(id+"F2.wireOp",EDGE,"E467"),sQuery(id+"F2.wireOp",EDGE,"E468"),sQuery(id+"F2.wireOp",EDGE,"E469"),sQuery(id+"F2.wireOp",EDGE,"E470"),sQuery(id+"F2.wireOp",EDGE,"E471"),sQuery(id+"F2.wireOp",EDGE,"E472"),sQuery(id+"F2.wireOp",EDGE,"E473"),sQuery(id+"F2.wireOp",EDGE,"E474"),sQuery(id+"F2.wireOp",EDGE,"E475"),sQuery(id+"F2.wireOp",EDGE,"E476"),sQuery(id+"F2.wireOp",EDGE,"E477"),sQuery(id+"F2.wireOp",EDGE,"E478"),sQuery(id+"F2.wireOp",EDGE,"E479"),sQuery(id+"F2.wireOp",EDGE,"E480"),sQuery(id+"F2.wireOp",EDGE,"E481"),sQuery(id+"F2.wireOp",EDGE,"E482"),sQuery(id+"F2.wireOp",EDGE,"E483"),sQuery(id+"F2.wireOp",EDGE,"E484"),sQuery(id+"F2.wireOp",EDGE,"E485"),sQuery(id+"F2.wireOp",EDGE,"E486"),sQuery(id+"F2.wireOp",EDGE,"E487"),sQuery(id+"F2.wireOp",EDGE,"E488"),sQuery(id+"F2.wireOp",EDGE,"E489"),sQuery(id+"F2.wireOp",EDGE,"E490"),sQuery(id+"F2.wireOp",EDGE,"E491"),sQuery(id+"F2.wireOp",EDGE,"E492"),sQuery(id+"F2.wireOp",EDGE,"E493"),sQuery(id+"F2.wireOp",EDGE,"E494"),sQuery(id+"F2.wireOp",EDGE,"E495"),sQuery(id+"F2.wireOp",EDGE,"E496"),sQuery(id+"F2.wireOp",EDGE,"E497"),sQuery(id+"F2.wireOp",EDGE,"E498"),sQuery(id+"F2.wireOp",EDGE,"E499"),sQuery(id+"F2.wireOp",EDGE,"E500"),sQuery(id+"F2.wireOp",EDGE,"E501"),sQuery(id+"F2.wireOp",EDGE,"E502"),sQuery(id+"F2.wireOp",EDGE,"E503"),sQuery(id+"F2.wireOp",EDGE,"E504"),sQuery(id+"F2.wireOp",EDGE,"E505"),sQuery(id+"F2.wireOp",EDGE,"E506"),sQuery(id+"F2.wireOp",EDGE,"E507"),sQuery(id+"F2.wireOp",EDGE,"E508"),sQuery(id+"F2.wireOp",EDGE,"E509"),sQuery(id+"F2.wireOp",EDGE,"E510"),sQuery(id+"F2.wireOp",EDGE,"E511"),sQuery(id+"F2.wireOp",EDGE,"E512"),sQuery(id+"F2.wireOp",EDGE,"E513"),sQuery(id+"F2.wireOp",EDGE,"E514"),sQuery(id+"F2.wireOp",EDGE,"E515"),sQuery(id+"F2.wireOp",EDGE,"E516"),sQuery(id+"F2.wireOp",EDGE,"E517"),sQuery(id+"F2.wireOp",EDGE,"E518"),sQuery(id+"F2.wireOp",EDGE,"E519"),sQuery(id+"F2.wireOp",EDGE,"E520"),sQuery(id+"F2.wireOp",EDGE,"E521"),sQuery(id+"F2.wireOp",EDGE,"E522"),sQuery(id+"F2.wireOp",EDGE,"E523"),sQuery(id+"F2.wireOp",EDGE,"E524"),sQuery(id+"F2.wireOp",EDGE,"E525"),sQuery(id+"F2.wireOp",EDGE,"E526"),sQuery(id+"F2.wireOp",EDGE,"E527"),sQuery(id+"F2.wireOp",EDGE,"E528"),sQuery(id+"F2.wireOp",EDGE,"E529"),sQuery(id+"F2.wireOp",EDGE,"E530"),sQuery(id+"F2.wireOp",EDGE,"E531"),sQuery(id+"F2.wireOp",EDGE,"E532"),sQuery(id+"F2.wireOp",EDGE,"E533"),sQuery(id+"F2.wireOp",EDGE,"E534"),sQuery(id+"F2.wireOp",EDGE,"E535"),sQuery(id+"F2.wireOp",EDGE,"E536"),sQuery(id+"F2.wireOp",EDGE,"E537"),sQuery(id+"F2.wireOp",EDGE,"E538"),sQuery(id+"F2.wireOp",EDGE,"E539"),sQuery(id+"F2.wireOp",EDGE,"E540"),sQuery(id+"F2.wireOp",EDGE,"E541"),sQuery(id+"F2.wireOp",EDGE,"E542"),sQuery(id+"F2.wireOp",EDGE,"E543"),sQuery(id+"F2.wireOp",EDGE,"E544"),sQuery(id+"F2.wireOp",EDGE,"E545"),sQuery(id+"F2.wireOp",EDGE,"E546"),sQuery(id+"F2.wireOp",EDGE,"E547"),sQuery(id+"F2.wireOp",EDGE,"E548"),sQuery(id+"F2.wireOp",EDGE,"E549"),sQuery(id+"F2.wireOp",EDGE,"E550"),sQuery(id+"F2.wireOp",EDGE,"E551"),sQuery(id+"F2.wireOp",EDGE,"E552"),sQuery(id+"F2.wireOp",EDGE,"E553"),sQuery(id+"F2.wireOp",EDGE,"E554"),sQuery(id+"F2.wireOp",EDGE,"E555"),sQuery(id+"F2.wireOp",EDGE,"E556"),sQuery(id+"F2.wireOp",EDGE,"E557"),sQuery(id+"F2.wireOp",EDGE,"E558"),sQuery(id+"F2.wireOp",EDGE,"E559"),sQuery(id+"F2.wireOp",EDGE,"E560"),sQuery(id+"F2.wireOp",EDGE,"E561"),sQuery(id+"F2.wireOp",EDGE,"E562")])]});
            var Q3;
            Q3=makeQuery(id+"F3.opExtrude","SWEPT_BODY",BODY,{"disambiguationData":[OSD([sQuery(id+"F2.wireOp",EDGE,"E563"),sQuery(id+"F2.wireOp",EDGE,"E564"),sQuery(id+"F2.wireOp",EDGE,"E565"),sQuery(id+"F2.wireOp",EDGE,"E566"),sQuery(id+"F2.wireOp",EDGE,"E567"),sQuery(id+"F2.wireOp",EDGE,"E568"),sQuery(id+"F2.wireOp",EDGE,"E569"),sQuery(id+"F2.wireOp",EDGE,"E570"),sQuery(id+"F2.wireOp",EDGE,"E571"),sQuery(id+"F2.wireOp",EDGE,"E572"),sQuery(id+"F2.wireOp",EDGE,"E573"),sQuery(id+"F2.wireOp",EDGE,"E574"),sQuery(id+"F2.wireOp",EDGE,"E575"),sQuery(id+"F2.wireOp",EDGE,"E576"),sQuery(id+"F2.wireOp",EDGE,"E577"),sQuery(id+"F2.wireOp",EDGE,"E578"),sQuery(id+"F2.wireOp",EDGE,"E579"),sQuery(id+"F2.wireOp",EDGE,"E580"),sQuery(id+"F2.wireOp",EDGE,"E581"),sQuery(id+"F2.wireOp",EDGE,"E582"),sQuery(id+"F2.wireOp",EDGE,"E583"),sQuery(id+"F2.wireOp",EDGE,"E584"),sQuery(id+"F2.wireOp",EDGE,"E585"),sQuery(id+"F2.wireOp",EDGE,"E586"),sQuery(id+"F2.wireOp",EDGE,"E587"),sQuery(id+"F2.wireOp",EDGE,"E588"),sQuery(id+"F2.wireOp",EDGE,"E589"),sQuery(id+"F2.wireOp",EDGE,"E590"),sQuery(id+"F2.wireOp",EDGE,"E591"),sQuery(id+"F2.wireOp",EDGE,"E592"),sQuery(id+"F2.wireOp",EDGE,"E593"),sQuery(id+"F2.wireOp",EDGE,"E594"),sQuery(id+"F2.wireOp",EDGE,"E595"),sQuery(id+"F2.wireOp",EDGE,"E596"),sQuery(id+"F2.wireOp",EDGE,"E597"),sQuery(id+"F2.wireOp",EDGE,"E598"),sQuery(id+"F2.wireOp",EDGE,"E599"),sQuery(id+"F2.wireOp",EDGE,"E600"),sQuery(id+"F2.wireOp",EDGE,"E601"),sQuery(id+"F2.wireOp",EDGE,"E602"),sQuery(id+"F2.wireOp",EDGE,"E603"),sQuery(id+"F2.wireOp",EDGE,"E604"),sQuery(id+"F2.wireOp",EDGE,"E605"),sQuery(id+"F2.wireOp",EDGE,"E606"),sQuery(id+"F2.wireOp",EDGE,"E607"),sQuery(id+"F2.wireOp",EDGE,"E608"),sQuery(id+"F2.wireOp",EDGE,"E609"),sQuery(id+"F2.wireOp",EDGE,"E610"),sQuery(id+"F2.wireOp",EDGE,"E611"),sQuery(id+"F2.wireOp",EDGE,"E612"),sQuery(id+"F2.wireOp",EDGE,"E613"),sQuery(id+"F2.wireOp",EDGE,"E614"),sQuery(id+"F2.wireOp",EDGE,"E615"),sQuery(id+"F2.wireOp",EDGE,"E616"),sQuery(id+"F2.wireOp",EDGE,"E617"),sQuery(id+"F2.wireOp",EDGE,"E618"),sQuery(id+"F2.wireOp",EDGE,"E619"),sQuery(id+"F2.wireOp",EDGE,"E620"),sQuery(id+"F2.wireOp",EDGE,"E621")])]});
            var Q4;
            Q4=makeQuery(id+"F3.opExtrude","SWEPT_BODY",BODY,{"disambiguationData":[OSD([sQuery(id+"F2.wireOp",EDGE,"E622"),sQuery(id+"F2.wireOp",EDGE,"E623"),sQuery(id+"F2.wireOp",EDGE,"E624"),sQuery(id+"F2.wireOp",EDGE,"E625")])]});
            var Q5;
            Q5=qCreatedBy(makeId("Origin.pointOp"),VERTEX);
            transform(context, id + "F4", {"entities" : qUnion([Q0, Q1, Q2, Q3, Q4]), "transformType" : TransformType.SCALE_UNIFORMLY, "scale" : 1, "scalePoint" : qUnion([Q5]), "makeCopy" : false});
        }
    });
